FCSTD DOCUMENT  (FreeCAD 0.17R13541 (Git))
Label: PCSchrank2
License: All rights reserved
LicenseURL: http://en.wikipedia.org/wiki/All_rights_reserved
objects: Drawing::FeatureViewPython×69, Drawing::FeatureViewPart×29, Part::Box×21, Drawing::FeaturePage×5, Part::Cylinder×4, App::Part×2, Part::FeaturePython×1
note: 26 computed .brp shape members not serialized (recipe doc carries the construction recipe); baked Part::Feature solids carry a one-line shape summary decoded from their .brp

FEATURE [Part::Box] Box  label="Boden"
  AttacherType = Attacher::AttachEngine3D
  Height = 19
  Length = 750
  Width = 300
FEATURE [Part::Box] Box001  label="Mittelebene"
  AttacherType = Attacher::AttachEngine3D
  Height = 19
  Length = 731
  Placement = pos=(0,0,700) rot=(0,0,1;0rad)
  Width = 300
FEATURE [Part::Box] Box002  label="Deckel"
  AttacherType = Attacher::AttachEngine3D
  Height = 19
  Length = 731
  Placement = pos=(0,0,1281) rot=(0,0,1;0rad)
  Width = 300
FEATURE [Part::Box] Box003  label="SeiteLi"
  AttacherType = Attacher::AttachEngine3D
  Height = 1300
  Length = 19
  Placement = pos=(-19,0,0) rot=(0,0,1;0rad)
  Width = 300
FEATURE [Part::Box] Box004  label="SeiteRe"
  AttacherType = Attacher::AttachEngine3D
  Height = 600
  Length = 19
  Placement = pos=(731,0,700) rot=(0,0,1;0rad)
  Width = 300
FEATURE [Part::Box] Box005  label="AbdeckungVo"
  AttacherType = Attacher::AttachEngine3D
  Height = 705
  Length = 550
  Placement = pos=(200,-19,0) rot=(0,0,1;0rad)
  Width = 19
FEATURE [Part::Box] Box006  label="Tuere"
  AttacherType = Attacher::AttachEngine3D
  Height = 705
  Length = 219
  Placement = pos=(-19,-19,0) rot=(0,0,1;0rad)
  Width = 19
FEATURE [Part::Box] Box007  label="StuetzeMi"
  AttacherType = Attacher::AttachEngine3D
  Height = 681
  Length = 19
  Placement = pos=(190,0,19) rot=(0,0,1;0rad)
  Width = 300
FEATURE [Part::Box] Box008  label="Klappe"
  AttacherType = Attacher::AttachEngine3D
  Height = 595
  Length = 769
  Placement = pos=(-19,-19,705) rot=(0,0,1;0rad)
  Width = 19
FEATURE [Part::Box] Box009  label="StuetzeHi"
  AttacherType = Attacher::AttachEngine3D
  Height = 681
  Length = 100
  Placement = pos=(650,281,19) rot=(0,0,1;0rad)
  Width = 19
FEATURE [Part::Cylinder] Cylinder  label="GriffTuere"
  Angle = 360
  AttacherType = Attacher::AttachEngine3D
  Height = 20
  Placement = pos=(160,-19,600) rot=(1,0,0;1.5708rad)
  Radius = 10
FEATURE [Part::Cylinder] Cylinder001  label="GriffKlappe"
  Angle = 360
  AttacherType = Attacher::AttachEngine3D
  Height = 20
  Placement = pos=(380,-19,1200) rot=(1,0,0;1.5708rad)
  Radius = 10
FEATURE [App::Part] Part
  Group = -> [Box,Box001,Box002,Box003,Box004,Box005,Box006,Box007,Box008,Box009,Cylinder,Cylinder001]
  License = CC BY 3.0
  LicenseURL = http://creativecommons.org/licenses/by/3.0/
  Origin = -> Origin
FEATURE [Part::Box] Box010  label="Boden001"
  AttacherType = Attacher::AttachEngine3D
  Height = 19
  Length = 750
  Width = 300
FEATURE [Part::Box] Box011  label="Mittelebene001"
  AttacherType = Attacher::AttachEngine3D
  Height = 19
  Length = 731
  Placement = pos=(0,0,700) rot=(0,0,1;0rad)
  Width = 300
FEATURE [Part::Box] Box012  label="Deckel001"
  AttacherType = Attacher::AttachEngine3D
  Height = 19
  Length = 731
  Placement = pos=(0,0,1281) rot=(0,0,1;0rad)
  Width = 300
FEATURE [Part::Box] Box013  label="SeiteLi001"
  AttacherType = Attacher::AttachEngine3D
  Height = 1300
  Length = 19
  Placement = pos=(-19,0,0) rot=(0,0,1;0rad)
  Width = 300
FEATURE [Part::Box] Box014  label="SeiteRe001"
  AttacherType = Attacher::AttachEngine3D
  Height = 600
  Length = 19
  Placement = pos=(731,0,700) rot=(0,0,1;0rad)
  Width = 300
FEATURE [Part::Box] Box015  label="AbdeckungVo001"
  AttacherType = Attacher::AttachEngine3D
  Height = 705
  Length = 550
  Placement = pos=(200,-19,0) rot=(0,0,1;0rad)
  Width = 19
FEATURE [Part::Box] Box016  label="Tuere001"
  AttacherType = Attacher::AttachEngine3D
  Height = 705
  Length = 219
  Placement = pos=(-19,-19,0) rot=(0,0,1;0rad)
  Width = 19
FEATURE [Part::Box] Box017  label="StuetzeMi001"
  AttacherType = Attacher::AttachEngine3D
  Height = 681
  Length = 19
  Placement = pos=(190,0,19) rot=(0,0,1;0rad)
  Width = 300
FEATURE [Part::Box] Box018  label="Klappe001"
  AttacherType = Attacher::AttachEngine3D
  Height = 595
  Length = 769
  Placement = pos=(-19,-19,705) rot=(0,0,1;0rad)
  Width = 19
FEATURE [Part::Box] Box019  label="StuetzeHi001"
  AttacherType = Attacher::AttachEngine3D
  Height = 681
  Length = 100
  Placement = pos=(650,281,19) rot=(0,0,1;0rad)
  Width = 19
FEATURE [Part::Cylinder] Cylinder002  label="GriffTuere001"
  Angle = 360
  AttacherType = Attacher::AttachEngine3D
  Height = 20
  Placement = pos=(160,-19,600) rot=(1,0,0;1.5708rad)
  Radius = 10
FEATURE [Part::Cylinder] Cylinder003  label="GriffKlappe001"
  Angle = 360
  AttacherType = Attacher::AttachEngine3D
  Height = 20
  Placement = pos=(380,-19,1200) rot=(1,0,0;1.5708rad)
  Radius = 10
FEATURE [App::Part] Part001
  Group = -> [Box010,Box011,Box012,Box013,Box014,Box015,Box016,Box017,Box018,Box019,Cylinder002,Cylinder003]
  License = CC BY 3.0
  LicenseURL = http://creativecommons.org/licenses/by/3.0/
  Origin = -> Origin001
FEATURE [Drawing::FeatureViewPart] Ortho  label="Ortho_0_0"
  Direction = (0,0,1)
  HiddenWidth = 0.15
  LineWidth = 0.35
  Rotation = 0
  Scale = 0.1
  ShowHiddenLines = false
  ShowSmoothLines = false
  Source = -> Box
  Tolerance = 0.05
  ViewResult = <g id="Ortho_0_0"\n   transform="rotate(0,32.5,55) translate(32.5,55) scale(0.1,0.1)"\n  >\n<g   fill="none"\n   stroke="rgb(0, 0, 0)"\n   stroke-linecap="butt"\n   stroke-linejoin="miter"\n   stroke-width="3.500000"\n   transform="scale(1,-1)"\n  >\n<path id= "1" d=" M 0 0 L 0 300 " />\n<path id= "2" d=" M 750 0 L 750 300 " />\n<path id= "3" d=" M 0 0 L 750 0 " />\n<path id= "4" d=" M 0 300 L 750 300 " />\n</g>\n</g>
  Visible = true
  X = 32.5
  Y = 55
FEATURE [Drawing::FeatureViewPython] dim001  # drawing view (typed FeaturePython)
  Rotation = 0
  ViewResult = <g> \n  <line x1="32.500000" y1="57.000000" x2="32.500000" y2="64.603174" style="stroke:rgb(0,0,255);stroke-width:0.50" />\n<line x1="107.500000" y1="57.000000" x2="107.500000" y2="64.603174" style="stroke:rgb(0,0,255);stroke-width:0.50" />\n<line x1="32.500000" y1="63.603174" x2="107.500000" y2="63.603174" style="stroke:rgb(0,0,255);stroke-width:0.50" /> \n  <polygon points="107.500000,63.603174 104.500000,62.603174 103.500000,63.603174 104.500000,64.603174" style="fill:rgb(0,0,255);stroke:rgb(0,0,255);stroke-width:0" /><polygon points="32.500000,63.603174 35.500000,64.603174 36.500000,63.603174 35.500000,62.603174" style="fill:rgb(0,0,255);stroke:rgb(0,0,255);stroke-width:0" /> \n  <text x="70.000000" y="61.603174" font-family="inherit" font-size="3.6" fill="rgb(0,0,255)" text-anchor="middle" transform="rotate(0.000000 70.000000,61.603174)" >750</text> </g>
  Visible = true
  X = 0
  Y = 0
  arrowL1 = 3
  arrowL2 = 1
  arrowW = 2
  arrow_scheme = 0
  autoPlaceOffset = 2
  autoPlaceText = true
  click1_x = 54.517
  click1_y = 63.6032
  click2_x = 54.517
  click2_y = 63.6032
  comma_decimal_place = false
  dimension_line_overshoot = 1
  gap_datum_points = 2
  halfDimension_linear = false
  lineColor = rgb(0,0,255)
  strokeWidth = 0.5
  textFormat_linear = %(value)3.3f
  textRenderer_color = rgb(0,0,255)
  textRenderer_family = inherit
  textRenderer_size = 3.6
  unit_custom_scale = 1
  unit_scheme = 0
FEATURE [Drawing::FeatureViewPython] dim002  # drawing view (typed FeaturePython)
  Rotation = 0
  ViewResult = <g> \n  <line x1="109.500000" y1="55.000000" x2="116.280753" y2="55.000000" style="stroke:rgb(0,0,255);stroke-width:0.50" />\n<line x1="109.500000" y1="25.000000" x2="116.280753" y2="25.000000" style="stroke:rgb(0,0,255);stroke-width:0.50" />\n<line x1="115.280753" y1="55.000000" x2="115.280753" y2="25.000000" style="stroke:rgb(0,0,255);stroke-width:0.50" /> \n  <polygon points="115.280753,25.000000 114.280753,28.000000 115.280753,29.000000 116.280753,28.000000" style="fill:rgb(0,0,255);stroke:rgb(0,0,255);stroke-width:0" /><polygon points="115.280753,55.000000 116.280753,52.000000 115.280753,51.000000 114.280753,52.000000" style="fill:rgb(0,0,255);stroke:rgb(0,0,255);stroke-width:0" /> \n  <text x="113.280753" y="40.000000" font-family="inherit" font-size="3.6" fill="rgb(0,0,255)" text-anchor="middle" transform="rotate(-90.000000 113.280753,40.000000)" >300</text> </g>
  Visible = true
  X = 0
  Y = 0
  arrowL1 = 3
  arrowL2 = 1
  arrowW = 2
  arrow_scheme = 0
  autoPlaceOffset = 2
  autoPlaceText = true
  click1_x = 115.281
  click1_y = 42.0235
  click2_x = 115.281
  click2_y = 42.0235
  comma_decimal_place = false
  dimension_line_overshoot = 1
  gap_datum_points = 2
  halfDimension_linear = false
  lineColor = rgb(0,0,255)
  strokeWidth = 0.5
  textFormat_linear = %(value)3.3f
  textRenderer_color = rgb(0,0,255)
  textRenderer_family = inherit
  textRenderer_size = 3.6
  unit_custom_scale = 1
  unit_scheme = 0
FEATURE [Drawing::FeatureViewPart] Ortho001  label="Ortho_0_001"
  Direction = (0,0,1)
  HiddenWidth = 0.15
  LineWidth = 0.35
  Rotation = 0
  Scale = 0.1
  ShowHiddenLines = false
  ShowSmoothLines = false
  Source = -> Box001
  Tolerance = 0.05
  ViewResult = <g id="Ortho_0_001"\n   transform="rotate(0,33.45,105) translate(33.45,105) scale(0.1,0.1)"\n  >\n<g   fill="none"\n   stroke="rgb(0, 0, 0)"\n   stroke-linecap="butt"\n   stroke-linejoin="miter"\n   stroke-width="3.500000"\n   transform="scale(1,-1)"\n  >\n<path id= "1" d=" M 0 0 L 0 300 " />\n<path id= "2" d=" M 731 0 L 731 300 " />\n<path id= "3" d=" M 0 0 L 731 0 " />\n<path id= "4" d=" M 0 300 L 731 300 " />\n</g>\n</g>
  Visible = true
  X = 33.45
  Y = 105
FEATURE [Drawing::FeatureViewPython] dim003  # drawing view (typed FeaturePython)
  Rotation = 0
  ViewResult = <g> \n  <line x1="33.450000" y1="107.000000" x2="33.450000" y2="114.577097" style="stroke:rgb(0,0,255);stroke-width:0.50" />\n<line x1="106.550000" y1="107.000000" x2="106.550000" y2="114.577097" style="stroke:rgb(0,0,255);stroke-width:0.50" />\n<line x1="33.450000" y1="113.577097" x2="106.550000" y2="113.577097" style="stroke:rgb(0,0,255);stroke-width:0.50" /> \n  <polygon points="106.550000,113.577097 103.550000,112.577097 102.550000,113.577097 103.550000,114.577097" style="fill:rgb(0,0,255);stroke:rgb(0,0,255);stroke-width:0" /><polygon points="33.450000,113.577097 36.450000,114.577097 37.450000,113.577097 36.450000,112.577097" style="fill:rgb(0,0,255);stroke:rgb(0,0,255);stroke-width:0" /> \n  <text x="70.000000" y="111.577097" font-family="inherit" font-size="3.6" fill="rgb(0,0,255)" text-anchor="middle" transform="rotate(0.000000 70.000000,111.577097)" >731</text> </g>
  Visible = true
  X = 0
  Y = 0
  arrowL1 = 3
  arrowL2 = 1
  arrowW = 2
  arrow_scheme = 0
  autoPlaceOffset = 2
  autoPlaceText = true
  click1_x = 56.2207
  click1_y = 113.577
  click2_x = 56.2207
  click2_y = 113.577
  comma_decimal_place = false
  dimension_line_overshoot = 1
  gap_datum_points = 2
  halfDimension_linear = false
  lineColor = rgb(0,0,255)
  strokeWidth = 0.5
  textFormat_linear = %(value)3.3f
  textRenderer_color = rgb(0,0,255)
  textRenderer_family = inherit
  textRenderer_size = 3.6
  unit_custom_scale = 1
  unit_scheme = 0
FEATURE [Drawing::FeatureViewPython] dim004  # drawing view (typed FeaturePython)
  Rotation = 0
  ViewResult = <g> \n  <line x1="108.550000" y1="105.000000" x2="116.848639" y2="105.000000" style="stroke:rgb(0,0,255);stroke-width:0.50" />\n<line x1="108.550000" y1="75.000000" x2="116.848639" y2="75.000000" style="stroke:rgb(0,0,255);stroke-width:0.50" />\n<line x1="115.848639" y1="105.000000" x2="115.848639" y2="75.000000" style="stroke:rgb(0,0,255);stroke-width:0.50" /> \n  <polygon points="115.848639,75.000000 114.848639,78.000000 115.848639,79.000000 116.848639,78.000000" style="fill:rgb(0,0,255);stroke:rgb(0,0,255);stroke-width:0" /><polygon points="115.848639,105.000000 116.848639,102.000000 115.848639,101.000000 114.848639,102.000000" style="fill:rgb(0,0,255);stroke:rgb(0,0,255);stroke-width:0" /> \n  <text x="113.848639" y="90.000000" font-family="inherit" font-size="3.6" fill="rgb(0,0,255)" text-anchor="middle" transform="rotate(-90.000000 113.848639,90.000000)" >300</text> </g>
  Visible = true
  X = 0
  Y = 0
  arrowL1 = 3
  arrowL2 = 1
  arrowW = 2
  arrow_scheme = 0
  autoPlaceOffset = 2
  autoPlaceText = true
  click1_x = 115.849
  click1_y = 87.4544
  click2_x = 115.849
  click2_y = 87.4544
  comma_decimal_place = false
  dimension_line_overshoot = 1
  gap_datum_points = 2
  halfDimension_linear = false
  lineColor = rgb(0,0,255)
  strokeWidth = 0.5
  textFormat_linear = %(value)3.3f
  textRenderer_color = rgb(0,0,255)
  textRenderer_family = inherit
  textRenderer_size = 3.6
  unit_custom_scale = 1
  unit_scheme = 0
FEATURE [Drawing::FeatureViewPart] Ortho002  label="Ortho_0_002"
  Direction = (0,0,1)
  HiddenWidth = 0.15
  LineWidth = 0.35
  Rotation = 0
  Scale = 0.1
  ShowHiddenLines = false
  ShowSmoothLines = false
  Source = -> Box002
  Tolerance = 0.05
  ViewResult = <g id="Ortho_0_002"\n   transform="rotate(0,33.45,155) translate(33.45,155) scale(0.1,0.1)"\n  >\n<g   fill="none"\n   stroke="rgb(0, 0, 0)"\n   stroke-linecap="butt"\n   stroke-linejoin="miter"\n   stroke-width="3.500000"\n   transform="scale(1,-1)"\n  >\n<path id= "1" d=" M 0 0 L 0 300 " />\n<path id= "2" d=" M 731 0 L 731 300 " />\n<path id= "3" d=" M 0 0 L 731 0 " />\n<path id= "4" d=" M 0 300 L 731 300 " />\n</g>\n</g>
  Visible = true
  X = 33.45
  Y = 155
FEATURE [Drawing::FeatureViewPython] dim005  # drawing view (typed FeaturePython)
  Rotation = 0
  ViewResult = <g> \n  <line x1="33.450000" y1="157.000000" x2="33.450000" y2="165.686790" style="stroke:rgb(0,0,255);stroke-width:0.50" />\n<line x1="106.550000" y1="157.000000" x2="106.550000" y2="165.686790" style="stroke:rgb(0,0,255);stroke-width:0.50" />\n<line x1="33.450000" y1="164.686790" x2="106.550000" y2="164.686790" style="stroke:rgb(0,0,255);stroke-width:0.50" /> \n  <polygon points="106.550000,164.686790 103.550000,163.686790 102.550000,164.686790 103.550000,165.686790" style="fill:rgb(0,0,255);stroke:rgb(0,0,255);stroke-width:0" /><polygon points="33.450000,164.686790 36.450000,165.686790 37.450000,164.686790 36.450000,163.686790" style="fill:rgb(0,0,255);stroke:rgb(0,0,255);stroke-width:0" /> \n  <text x="70.000000" y="162.686790" font-family="inherit" font-size="3.6" fill="rgb(0,0,255)" text-anchor="middle" transform="rotate(0.000000 70.000000,162.686790)" >731</text> </g>
  Visible = true
  X = 0
  Y = 0
  arrowL1 = 3
  arrowL2 = 1
  arrowW = 2
  arrow_scheme = 0
  autoPlaceOffset = 2
  autoPlaceText = true
  click1_x = 62.4674
  click1_y = 164.687
  click2_x = 62.4674
  click2_y = 164.687
  comma_decimal_place = false
  dimension_line_overshoot = 1
  gap_datum_points = 2
  halfDimension_linear = false
  lineColor = rgb(0,0,255)
  strokeWidth = 0.5
  textFormat_linear = %(value)3.3f
  textRenderer_color = rgb(0,0,255)
  textRenderer_family = inherit
  textRenderer_size = 3.6
  unit_custom_scale = 1
  unit_scheme = 0
FEATURE [Drawing::FeatureViewPython] dim006  # drawing view (typed FeaturePython)
  Rotation = 0
  ViewResult = <g> \n  <line x1="108.550000" y1="155.000000" x2="116.848639" y2="155.000000" style="stroke:rgb(0,0,255);stroke-width:0.50" />\n<line x1="108.550000" y1="125.000000" x2="116.848639" y2="125.000000" style="stroke:rgb(0,0,255);stroke-width:0.50" />\n<line x1="115.848639" y1="155.000000" x2="115.848639" y2="125.000000" style="stroke:rgb(0,0,255);stroke-width:0.50" /> \n  <polygon points="115.848639,125.000000 114.848639,128.000000 115.848639,129.000000 116.848639,128.000000" style="fill:rgb(0,0,255);stroke:rgb(0,0,255);stroke-width:0" /><polygon points="115.848639,155.000000 116.848639,152.000000 115.848639,151.000000 114.848639,152.000000" style="fill:rgb(0,0,255);stroke:rgb(0,0,255);stroke-width:0" /> \n  <text x="113.848639" y="140.000000" font-family="inherit" font-size="3.6" fill="rgb(0,0,255)" text-anchor="middle" transform="rotate(-90.000000 113.848639,140.000000)" >300</text> </g>
  Visible = true
  X = 0
  Y = 0
  arrowL1 = 3
  arrowL2 = 1
  arrowW = 2
  arrow_scheme = 0
  autoPlaceOffset = 2
  autoPlaceText = true
  click1_x = 115.849
  click1_y = 140.836
  click2_x = 115.849
  click2_y = 140.836
  comma_decimal_place = false
  dimension_line_overshoot = 1
  gap_datum_points = 2
  halfDimension_linear = false
  lineColor = rgb(0,0,255)
  strokeWidth = 0.5
  textFormat_linear = %(value)3.3f
  textRenderer_color = rgb(0,0,255)
  textRenderer_family = inherit
  textRenderer_size = 3.6
  unit_custom_scale = 1
  unit_scheme = 0
FEATURE [Drawing::FeatureViewPart] Ortho003  label="Ortho_0_003"
  Direction = (1,0,0)
  HiddenWidth = 0.15
  LineWidth = 0.35
  Rotation = -90
  Scale = 0.1
  ShowHiddenLines = false
  ShowSmoothLines = false
  Source = -> Box003
  Tolerance = 0.05
  ViewResult = <g id="Ortho_0_003"\n   transform="rotate(-90,145,155) translate(145,155) scale(0.1,0.1)"\n  >\n<g   fill="none"\n   stroke="rgb(0, 0, 0)"\n   stroke-linecap="butt"\n   stroke-linejoin="miter"\n   stroke-width="3.500000"\n   transform="scale(1,-1)"\n  >\n<path id= "1" d=" M 0 0 L 1300 0 " />\n<path id= "2" d=" M 1300 0 L 1300 -300 " />\n<path id= "3" d=" M 0 -300 L 1300 -300 " />\n<path id= "4" d=" M 0 0 L 0 -300 " />\n</g>\n</g>
  Visible = true
  X = 145
  Y = 155
FEATURE [Drawing::FeatureViewPython] dim007  # drawing view (typed FeaturePython)
  Rotation = 0
  ViewResult = <g> \n  <line x1="145.000000" y1="157.000000" x2="145.000000" y2="166.254676" style="stroke:rgb(0,0,255);stroke-width:0.50" />\n<line x1="175.000000" y1="157.000000" x2="175.000000" y2="166.254676" style="stroke:rgb(0,0,255);stroke-width:0.50" />\n<line x1="145.000000" y1="165.254676" x2="175.000000" y2="165.254676" style="stroke:rgb(0,0,255);stroke-width:0.50" /> \n  <polygon points="175.000000,165.254676 172.000000,164.254676 171.000000,165.254676 172.000000,166.254676" style="fill:rgb(0,0,255);stroke:rgb(0,0,255);stroke-width:0" /><polygon points="145.000000,165.254676 148.000000,166.254676 149.000000,165.254676 148.000000,164.254676" style="fill:rgb(0,0,255);stroke:rgb(0,0,255);stroke-width:0" /> \n  <text x="160.000000" y="163.254676" font-family="inherit" font-size="3.6" fill="rgb(0,0,255)" text-anchor="middle" transform="rotate(0.000000 160.000000,163.254676)" >300</text> </g>
  Visible = true
  X = 0
  Y = 0
  arrowL1 = 3
  arrowL2 = 1
  arrowW = 2
  arrow_scheme = 0
  autoPlaceOffset = 2
  autoPlaceText = true
  click1_x = 159.008
  click1_y = 165.255
  click2_x = 159.008
  click2_y = 165.255
  comma_decimal_place = false
  dimension_line_overshoot = 1
  gap_datum_points = 2
  halfDimension_linear = false
  lineColor = rgb(0,0,255)
  strokeWidth = 0.5
  textFormat_linear = %(value)3.3f
  textRenderer_color = rgb(0,0,255)
  textRenderer_family = inherit
  textRenderer_size = 3.6
  unit_custom_scale = 1
  unit_scheme = 0
FEATURE [Drawing::FeatureViewPython] dim008  # drawing view (typed FeaturePython)
  Rotation = 0
  ViewResult = <g> \n  <line x1="177.000000" y1="155.000000" x2="186.698553" y2="155.000000" style="stroke:rgb(0,0,255);stroke-width:0.50" />\n<line x1="177.000000" y1="25.000000" x2="186.698553" y2="25.000000" style="stroke:rgb(0,0,255);stroke-width:0.50" />\n<line x1="185.698553" y1="155.000000" x2="185.698553" y2="25.000000" style="stroke:rgb(0,0,255);stroke-width:0.50" /> \n  <polygon points="185.698553,25.000000 184.698553,28.000000 185.698553,29.000000 186.698553,28.000000" style="fill:rgb(0,0,255);stroke:rgb(0,0,255);stroke-width:0" /><polygon points="185.698553,155.000000 186.698553,152.000000 185.698553,151.000000 184.698553,152.000000" style="fill:rgb(0,0,255);stroke:rgb(0,0,255);stroke-width:0" /> \n  <text x="183.698553" y="90.000000" font-family="inherit" font-size="3.6" fill="rgb(0,0,255)" text-anchor="middle" transform="rotate(-90.000000 183.698553,90.000000)" >1300</text> </g>
  Visible = true
  X = 0
  Y = 0
  arrowL1 = 3
  arrowL2 = 1
  arrowW = 2
  arrow_scheme = 0
  autoPlaceOffset = 2
  autoPlaceText = true
  click1_x = 185.699
  click1_y = 129.478
  click2_x = 185.699
  click2_y = 129.478
  comma_decimal_place = false
  dimension_line_overshoot = 1
  gap_datum_points = 2
  halfDimension_linear = false
  lineColor = rgb(0,0,255)
  strokeWidth = 0.5
  textFormat_linear = %(value)3.3f
  textRenderer_color = rgb(0,0,255)
  textRenderer_family = inherit
  textRenderer_size = 3.6
  unit_custom_scale = 1
  unit_scheme = 0
FEATURE [Drawing::FeatureViewPart] Ortho004  label="Ortho_0_004"
  Direction = (1,0,0)
  HiddenWidth = 0.15
  LineWidth = 0.35
  Rotation = 0
  Scale = 0.1
  ShowHiddenLines = false
  ShowSmoothLines = false
  Source = -> Box004
  Tolerance = 0.05
  ViewResult = <g id="Ortho_0_004"\n   transform="rotate(0,50,175) translate(50,175) scale(0.1,0.1)"\n  >\n<g   fill="none"\n   stroke="rgb(0, 0, 0)"\n   stroke-linecap="butt"\n   stroke-linejoin="miter"\n   stroke-width="3.500000"\n   transform="scale(1,-1)"\n  >\n<path id= "1" d=" M 700 0 L 1300 0 " />\n<path id= "2" d=" M 1300 0 L 1300 -300 " />\n<path id= "3" d=" M 700 -300 L 1300 -300 " />\n<path id= "4" d=" M 700 0 L 700 -300 " />\n</g>\n</g>
  Visible = true
  X = 50
  Y = 175
FEATURE [Drawing::FeatureViewPython] dim009  # drawing view (typed FeaturePython)
  Rotation = 0
  ViewResult = <g> \n  <line x1="120.000000" y1="207.000000" x2="120.000000" y2="213.389171" style="stroke:rgb(0,0,255);stroke-width:0.50" />\n<line x1="180.000000" y1="207.000000" x2="180.000000" y2="213.389171" style="stroke:rgb(0,0,255);stroke-width:0.50" />\n<line x1="120.000000" y1="212.389171" x2="180.000000" y2="212.389171" style="stroke:rgb(0,0,255);stroke-width:0.50" /> \n  <polygon points="180.000000,212.389171 177.000000,211.389171 176.000000,212.389171 177.000000,213.389171" style="fill:rgb(0,0,255);stroke:rgb(0,0,255);stroke-width:0" /><polygon points="120.000000,212.389171 123.000000,213.389171 124.000000,212.389171 123.000000,211.389171" style="fill:rgb(0,0,255);stroke:rgb(0,0,255);stroke-width:0" /> \n  <text x="150.000000" y="210.389171" font-family="inherit" font-size="3.6" fill="rgb(0,0,255)" text-anchor="middle" transform="rotate(0.000000 150.000000,210.389171)" >600</text> </g>
  Visible = true
  X = 0
  Y = 0
  arrowL1 = 3
  arrowL2 = 1
  arrowW = 2
  arrow_scheme = 0
  autoPlaceOffset = 2
  autoPlaceText = true
  click1_x = 140.836
  click1_y = 212.389
  click2_x = 140.836
  click2_y = 212.389
  comma_decimal_place = false
  dimension_line_overshoot = 1
  gap_datum_points = 2
  halfDimension_linear = false
  lineColor = rgb(0,0,255)
  strokeWidth = 0.5
  textFormat_linear = %(value)3.3f
  textRenderer_color = rgb(0,0,255)
  textRenderer_family = inherit
  textRenderer_size = 3.6
  unit_custom_scale = 1
  unit_scheme = 0
FEATURE [Drawing::FeatureViewPython] dim010  # drawing view (typed FeaturePython)
  Rotation = 0
  ViewResult = <g> \n  <line x1="182.000000" y1="175.000000" x2="190.673751" y2="175.000000" style="stroke:rgb(0,0,255);stroke-width:0.50" />\n<line x1="182.000000" y1="205.000000" x2="190.673751" y2="205.000000" style="stroke:rgb(0,0,255);stroke-width:0.50" />\n<line x1="189.673751" y1="175.000000" x2="189.673751" y2="205.000000" style="stroke:rgb(0,0,255);stroke-width:0.50" /> \n  <polygon points="189.673751,205.000000 190.673751,202.000000 189.673751,201.000000 188.673751,202.000000" style="fill:rgb(0,0,255);stroke:rgb(0,0,255);stroke-width:0" /><polygon points="189.673751,175.000000 188.673751,178.000000 189.673751,179.000000 190.673751,178.000000" style="fill:rgb(0,0,255);stroke:rgb(0,0,255);stroke-width:0" /> \n  <text x="187.673751" y="190.000000" font-family="inherit" font-size="3.6" fill="rgb(0,0,255)" text-anchor="middle" transform="rotate(-90.000000 187.673751,190.000000)" >300</text> </g>
  Visible = true
  X = 0
  Y = 0
  arrowL1 = 3
  arrowL2 = 1
  arrowW = 2
  arrow_scheme = 0
  autoPlaceOffset = 2
  autoPlaceText = true
  click1_x = 189.674
  click1_y = 191.377
  click2_x = 189.674
  click2_y = 191.377
  comma_decimal_place = false
  dimension_line_overshoot = 1
  gap_datum_points = 2
  halfDimension_linear = false
  lineColor = rgb(0,0,255)
  strokeWidth = 0.5
  textFormat_linear = %(value)3.3f
  textRenderer_color = rgb(0,0,255)
  textRenderer_family = inherit
  textRenderer_size = 3.6
  unit_custom_scale = 1
  unit_scheme = 0
FEATURE [Drawing::FeatureViewPython] text001  # drawing view (typed FeaturePython)
  Rotation = 0
  ViewResult = <g> <text x="52.245464" y="41.455640" font-family="inherit" font-size="5" fill="rgb(0,0,0)" text-anchor="inherit" transform="rotate(0.000000 52.245464,41.455640)" >Boden</text> </g>
  Visible = true
  X = 0
  Y = 0
  click1_x = 52.2455
  click1_y = 41.4556
  rotation = 0
  text = Boden
  textRenderer_addText_color = rgb(0,0,0)
  textRenderer_addText_family = inherit
  textRenderer_addText_size = 5
FEATURE [Drawing::FeatureViewPython] text002  # drawing view (typed FeaturePython)
  Rotation = 0
  ViewResult = <g> <text x="53.949121" y="90.293792" font-family="inherit" font-size="5" fill="rgb(0,0,0)" text-anchor="inherit" transform="rotate(0.000000 53.949121,90.293792)" >Mittelboden</text> </g>
  Visible = true
  X = 0
  Y = 0
  click1_x = 53.9491
  click1_y = 90.2938
  rotation = 0
  text = Mittelboden
  textRenderer_addText_color = rgb(0,0,0)
  textRenderer_addText_family = inherit
  textRenderer_addText_size = 5
FEATURE [Drawing::FeatureViewPython] text003  # drawing view (typed FeaturePython)
  Rotation = 0
  ViewResult = <g> <text x="56.220663" y="140.267714" font-family="inherit" font-size="5" fill="rgb(0,0,0)" text-anchor="inherit" transform="rotate(0.000000 56.220663,140.267714)" >Deckel</text> </g>
  Visible = true
  X = 0
  Y = 0
  click1_x = 56.2207
  click1_y = 140.268
  rotation = 0
  text = Deckel
  textRenderer_addText_color = rgb(0,0,0)
  textRenderer_addText_family = inherit
  textRenderer_addText_size = 5
FEATURE [Drawing::FeatureViewPython] text004  # drawing view (typed FeaturePython)
  Rotation = 0
  ViewResult = <g> <text x="160.000000" y="110.000000" font-family="inherit" font-size="5" fill="rgb(0,0,0)" text-anchor="inherit" transform="rotate(270.000000 160.000000,110.000000)" >Seitenwand links</text> </g>
  Visible = true
  X = 0
  Y = 0
  click1_x = 160
  click1_y = 110
  rotation = 270
  text = Seitenwand links
  textRenderer_addText_color = rgb(0,0,0)
  textRenderer_addText_family = inherit
  textRenderer_addText_size = 5
FEATURE [Drawing::FeatureViewPython] text005  # drawing view (typed FeaturePython)
  Rotation = 0
  ViewResult = <g> <text x="130.000000" y="190.000000" font-family="inherit" font-size="5" fill="rgb(0,0,0)" text-anchor="inherit" transform="rotate(0.000000 130.000000,190.000000)" >Seitenwand rechts</text> </g>
  Visible = true
  X = 0
  Y = 0
  click1_x = 130
  click1_y = 190
  rotation = 0
  text = Seitenwand rechts
  textRenderer_addText_color = rgb(0,0,0)
  textRenderer_addText_family = inherit
  textRenderer_addText_size = 5
FEATURE [Drawing::FeaturePage] Page  label="Seite"
  EditableTexts = Manuel Dillmann	 | PC-Schrank | Böden  | Seitenwände | A4 | 1 / X | 0.1 | ... | ... | 17/04/2019 | REV A
  Group = -> [Ortho,dim001,dim002,Ortho001,dim003,dim004,Ortho002,dim005,dim006,Ortho003,dim007,dim008,Ortho004,dim009,dim010,text001,text002,text003,text004,text005]
  Template = C:/Program Files/FreeCAD 0.17/data/Mod/Drawing/Templates/A4_Portrait_ISO7200.svg
FEATURE [Drawing::FeatureViewPart] Ortho005  label="Ortho_0_005"
  Direction = (0,1,0)
  HiddenWidth = 0.15
  LineWidth = 0.35
  Rotation = 90
  Scale = 0.1
  ShowHiddenLines = false
  ShowSmoothLines = false
  Source = -> Box005
  Tolerance = 0.05
  ViewResult = <g id="Ortho_0_005"\n   transform="rotate(90,12.5,24.75) translate(12.5,24.75) scale(0.1,0.1)"\n  >\n<g   fill="none"\n   stroke="rgb(0, 0, 0)"\n   stroke-linecap="butt"\n   stroke-linejoin="miter"\n   stroke-width="3.500000"\n   transform="scale(1,-1)"\n  >\n<path id= "1" d=" M 0 200 L 705 200 " />\n<path id= "2" d=" M 0 750 L 705 750 " />\n<path id= "3" d=" M 0 200 L 0 750 " />\n<path id= "4" d=" M 705 200 L 705 750 " />\n</g>\n</g>
  Visible = true
  X = 12.5
  Y = 24.75
FEATURE [Drawing::FeatureViewPython] dim011  # drawing view (typed FeaturePython)
  Rotation = 0
  ViewResult = <g> \n  <line x1="32.500000" y1="97.250000" x2="32.500000" y2="106.626700" style="stroke:rgb(0,0,255);stroke-width:0.50" />\n<line x1="87.500000" y1="97.250000" x2="87.500000" y2="106.626700" style="stroke:rgb(0,0,255);stroke-width:0.50" />\n<line x1="32.500000" y1="105.626700" x2="87.500000" y2="105.626700" style="stroke:rgb(0,0,255);stroke-width:0.50" /> \n  <polygon points="87.500000,105.626700 84.500000,104.626700 83.500000,105.626700 84.500000,106.626700" style="fill:rgb(0,0,255);stroke:rgb(0,0,255);stroke-width:0" /><polygon points="32.500000,105.626700 35.500000,106.626700 36.500000,105.626700 35.500000,104.626700" style="fill:rgb(0,0,255);stroke:rgb(0,0,255);stroke-width:0" /> \n  <text x="60.000000" y="103.626700" font-family="inherit" font-size="3.6" fill="rgb(0,0,255)" text-anchor="middle" transform="rotate(0.000000 60.000000,103.626700)" >550</text> </g>
  Visible = true
  X = 0
  Y = 0
  arrowL1 = 3
  arrowL2 = 1
  arrowW = 2
  arrow_scheme = 0
  autoPlaceOffset = 2
  autoPlaceText = true
  click1_x = 52.2455
  click1_y = 105.627
  click2_x = 52.2455
  click2_y = 105.627
  comma_decimal_place = false
  dimension_line_overshoot = 1
  gap_datum_points = 2
  halfDimension_linear = false
  lineColor = rgb(0,0,255)
  strokeWidth = 0.5
  textFormat_linear = %(value)3.3f
  textRenderer_color = rgb(0,0,255)
  textRenderer_family = inherit
  textRenderer_size = 3.6
  unit_custom_scale = 1
  unit_scheme = 0
FEATURE [Drawing::FeatureViewPython] dim012  # drawing view (typed FeaturePython)
  Rotation = 0
  ViewResult = <g> \n  <line x1="89.500000" y1="24.750000" x2="99.244189" y2="24.750000" style="stroke:rgb(0,0,255);stroke-width:0.50" />\n<line x1="89.500000" y1="95.250000" x2="99.244189" y2="95.250000" style="stroke:rgb(0,0,255);stroke-width:0.50" />\n<line x1="98.244189" y1="24.750000" x2="98.244189" y2="95.250000" style="stroke:rgb(0,0,255);stroke-width:0.50" /> \n  <polygon points="98.244189,95.250000 99.244189,92.250000 98.244189,91.250000 97.244189,92.250000" style="fill:rgb(0,0,255);stroke:rgb(0,0,255);stroke-width:0" /><polygon points="98.244189,24.750000 97.244189,27.750000 98.244189,28.750000 99.244189,27.750000" style="fill:rgb(0,0,255);stroke:rgb(0,0,255);stroke-width:0" /> \n  <text x="96.244189" y="60.000000" font-family="inherit" font-size="3.6" fill="rgb(0,0,255)" text-anchor="middle" transform="rotate(-90.000000 96.244189,60.000000)" >705</text> </g>
  Visible = true
  X = 0
  Y = 0
  arrowL1 = 3
  arrowL2 = 1
  arrowW = 2
  arrow_scheme = 0
  autoPlaceOffset = 2
  autoPlaceText = true
  click1_x = 98.2442
  click1_y = 77.2324
  click2_x = 98.2442
  click2_y = 77.2324
  comma_decimal_place = false
  dimension_line_overshoot = 1
  gap_datum_points = 2
  halfDimension_linear = false
  lineColor = rgb(0,0,255)
  strokeWidth = 0.5
  textFormat_linear = %(value)3.3f
  textRenderer_color = rgb(0,0,255)
  textRenderer_family = inherit
  textRenderer_size = 3.6
  unit_custom_scale = 1
  unit_scheme = 0
FEATURE [Drawing::FeatureViewPython] text006  # drawing view (typed FeaturePython)
  Rotation = 0
  ViewResult = <g> <text x="60.000000" y="90.000000" font-family="inherit" font-size="5" fill="rgb(0,0,0)" text-anchor="inherit" transform="rotate(270.000000 60.000000,90.000000)" >Abdeckung vorne unten</text> </g>
  Visible = true
  X = 0
  Y = 0
  click1_x = 60
  click1_y = 90
  rotation = 270
  text = Abdeckung vorne unten
  textRenderer_addText_color = rgb(0,0,0)
  textRenderer_addText_family = inherit
  textRenderer_addText_size = 5
FEATURE [Drawing::FeatureViewPart] Ortho006  label="Ortho_0_006"
  Direction = (0,1,0)
  HiddenWidth = 0.15
  LineWidth = 0.35
  Rotation = 90
  Scale = 0.1
  ShowHiddenLines = false
  ShowSmoothLines = false
  Source = -> Box006
  Tolerance = 0.05
  ViewResult = <g id="Ortho_0_006"\n   transform="rotate(90,110,24.75) translate(110,24.75) scale(0.1,0.1)"\n  >\n<g   fill="none"\n   stroke="rgb(0, 0, 0)"\n   stroke-linecap="butt"\n   stroke-linejoin="miter"\n   stroke-width="3.500000"\n   transform="scale(1,-1)"\n  >\n<path id= "1" d=" M 0 -19 L 705 -19 " />\n<path id= "2" d=" M 0 200 L 705 200 " />\n<path id= "3" d=" M 0 -19 L 0 200 " />\n<path id= "4" d=" M 705 -19 L 705 200 " />\n</g>\n</g>
  Visible = true
  X = 110
  Y = 24.75
FEATURE [Drawing::FeatureViewPython] text007  # drawing view (typed FeaturePython)
  Rotation = 0
  ViewResult = <g> <text x="120.000000" y="70.000000" font-family="inherit" font-size="5" fill="rgb(0,0,0)" text-anchor="inherit" transform="rotate(270.000000 120.000000,70.000000)" >Türe</text> </g>
  Visible = true
  X = 0
  Y = 0
  click1_x = 120
  click1_y = 70
  rotation = 270
  text = Türe
  textRenderer_addText_color = rgb(0,0,0)
  textRenderer_addText_family = inherit
  textRenderer_addText_size = 5
FEATURE [Drawing::FeatureViewPart] Ortho007  label="Ortho_0_007"
  Direction = (1,0,0)
  HiddenWidth = 0.15
  LineWidth = 0.35
  Rotation = -90
  Scale = 0.1
  ShowHiddenLines = false
  ShowSmoothLines = false
  Source = -> Box007
  Tolerance = 0.05
  ViewResult = <g id="Ortho_0_007"\n   transform="rotate(-90,35,190.95) translate(35,190.95) scale(0.1,0.1)"\n  >\n<g   fill="none"\n   stroke="rgb(0, 0, 0)"\n   stroke-linecap="butt"\n   stroke-linejoin="miter"\n   stroke-width="3.500000"\n   transform="scale(1,-1)"\n  >\n<path id= "1" d=" M 19 0 L 700 0 " />\n<path id= "2" d=" M 700 0 L 700 -300 " />\n<path id= "3" d=" M 19 -300 L 700 -300 " />\n<path id= "4" d=" M 19 0 L 19 -300 " />\n</g>\n</g>
  Visible = true
  X = 35
  Y = 190.95
FEATURE [Drawing::FeatureViewPython] dim015  # drawing view (typed FeaturePython)
  Rotation = 0
  ViewResult = <g> \n  <line x1="35.000000" y1="191.050000" x2="35.000000" y2="200.895690" style="stroke:rgb(0,0,255);stroke-width:0.50" />\n<line x1="65.000000" y1="191.050000" x2="65.000000" y2="200.895690" style="stroke:rgb(0,0,255);stroke-width:0.50" />\n<line x1="35.000000" y1="199.895690" x2="65.000000" y2="199.895690" style="stroke:rgb(0,0,255);stroke-width:0.50" /> \n  <polygon points="65.000000,199.895690 62.000000,198.895690 61.000000,199.895690 62.000000,200.895690" style="fill:rgb(0,0,255);stroke:rgb(0,0,255);stroke-width:0" /><polygon points="35.000000,199.895690 38.000000,200.895690 39.000000,199.895690 38.000000,198.895690" style="fill:rgb(0,0,255);stroke:rgb(0,0,255);stroke-width:0" /> \n  <text x="50.000000" y="197.895690" font-family="inherit" font-size="3.6" fill="rgb(0,0,255)" text-anchor="middle" transform="rotate(0.000000 50.000000,197.895690)" >300</text> </g>
  Visible = true
  X = 0
  Y = 0
  arrowL1 = 3
  arrowL2 = 1
  arrowW = 2
  arrow_scheme = 0
  autoPlaceOffset = 2
  autoPlaceText = true
  click1_x = 48.2703
  click1_y = 199.896
  click2_x = 48.2703
  click2_y = 199.896
  comma_decimal_place = false
  dimension_line_overshoot = 1
  gap_datum_points = 2
  halfDimension_linear = false
  lineColor = rgb(0,0,255)
  strokeWidth = 0.5
  textFormat_linear = %(value)3.3f
  textRenderer_color = rgb(0,0,255)
  textRenderer_family = inherit
  textRenderer_size = 3.6
  unit_custom_scale = 1
  unit_scheme = 0
FEATURE [Drawing::FeatureViewPython] dim016  # drawing view (typed FeaturePython)
  Rotation = 0
  ViewResult = <g> \n  <line x1="67.000000" y1="189.050000" x2="75.960884" y2="189.050000" style="stroke:rgb(0,0,255);stroke-width:0.50" />\n<line x1="67.000000" y1="120.950000" x2="75.960884" y2="120.950000" style="stroke:rgb(0,0,255);stroke-width:0.50" />\n<line x1="74.960884" y1="189.050000" x2="74.960884" y2="120.950000" style="stroke:rgb(0,0,255);stroke-width:0.50" /> \n  <polygon points="74.960884,120.950000 73.960884,123.950000 74.960884,124.950000 75.960884,123.950000" style="fill:rgb(0,0,255);stroke:rgb(0,0,255);stroke-width:0" /><polygon points="74.960884,189.050000 75.960884,186.050000 74.960884,185.050000 73.960884,186.050000" style="fill:rgb(0,0,255);stroke:rgb(0,0,255);stroke-width:0" /> \n  <text x="72.960884" y="155.000000" font-family="inherit" font-size="3.6" fill="rgb(0,0,255)" text-anchor="middle" transform="rotate(-90.000000 72.960884,155.000000)" >681</text> </g>
  Visible = true
  X = 0
  Y = 0
  arrowL1 = 3
  arrowL2 = 1
  arrowW = 2
  arrow_scheme = 0
  autoPlaceOffset = 2
  autoPlaceText = true
  click1_x = 74.9609
  click1_y = 162.983
  click2_x = 74.9609
  click2_y = 162.983
  comma_decimal_place = false
  dimension_line_overshoot = 1
  gap_datum_points = 2
  halfDimension_linear = false
  lineColor = rgb(0,0,255)
  strokeWidth = 0.5
  textFormat_linear = %(value)3.3f
  textRenderer_color = rgb(0,0,255)
  textRenderer_family = inherit
  textRenderer_size = 3.6
  unit_custom_scale = 1
  unit_scheme = 0
FEATURE [Drawing::FeatureViewPython] text008  # drawing view (typed FeaturePython)
  Rotation = 0
  ViewResult = <g> <text x="51.000000" y="183.000000" font-family="inherit" font-size="5" fill="rgb(0,0,0)" text-anchor="inherit" transform="rotate(270.000000 51.000000,183.000000)" >Stütze mitte (Trennwand)</text> </g>
  Visible = true
  X = 0
  Y = 0
  click1_x = 51
  click1_y = 183
  rotation = 270
  text = Stütze mitte (Trennwand)
  textRenderer_addText_color = rgb(0,0,0)
  textRenderer_addText_family = inherit
  textRenderer_addText_size = 5
FEATURE [Drawing::FeatureViewPart] Ortho008  label="Ortho_0_008"
  Direction = (0,1,0)
  HiddenWidth = 0.15
  LineWidth = 0.35
  Rotation = 90
  Scale = 0.1
  ShowHiddenLines = false
  ShowSmoothLines = false
  Source = -> Box008
  Tolerance = 0.05
  ViewResult = <g id="Ortho_0_008"\n   transform="rotate(90,93.45,49.75) translate(93.45,49.75) scale(0.1,0.1)"\n  >\n<g   fill="none"\n   stroke="rgb(0, 0, 0)"\n   stroke-linecap="butt"\n   stroke-linejoin="miter"\n   stroke-width="3.500000"\n   transform="scale(1,-1)"\n  >\n<path id= "1" d=" M 705 -19 L 1300 -19 " />\n<path id= "2" d=" M 705 750 L 1300 750 " />\n<path id= "3" d=" M 705 -19 L 705 750 " />\n<path id= "4" d=" M 1300 -19 L 1300 750 " />\n</g>\n</g>
  Visible = true
  X = 93.45
  Y = 49.75
FEATURE [Drawing::FeatureViewPython] dim017  # drawing view (typed FeaturePython)
  Rotation = 0
  ViewResult = <g> \n  <line x1="91.550000" y1="181.750000" x2="91.550000" y2="191.241637" style="stroke:rgb(0,0,255);stroke-width:0.50" />\n<line x1="168.450000" y1="181.750000" x2="168.450000" y2="191.241637" style="stroke:rgb(0,0,255);stroke-width:0.50" />\n<line x1="91.550000" y1="190.241637" x2="168.450000" y2="190.241637" style="stroke:rgb(0,0,255);stroke-width:0.50" /> \n  <polygon points="168.450000,190.241637 165.450000,189.241637 164.450000,190.241637 165.450000,191.241637" style="fill:rgb(0,0,255);stroke:rgb(0,0,255);stroke-width:0" /><polygon points="91.550000,190.241637 94.550000,191.241637 95.550000,190.241637 94.550000,189.241637" style="fill:rgb(0,0,255);stroke:rgb(0,0,255);stroke-width:0" /> \n  <text x="130.000000" y="188.241637" font-family="inherit" font-size="3.6" fill="rgb(0,0,255)" text-anchor="middle" transform="rotate(0.000000 130.000000,188.241637)" >769</text> </g>
  Visible = true
  X = 0
  Y = 0
  arrowL1 = 3
  arrowL2 = 1
  arrowW = 2
  arrow_scheme = 0
  autoPlaceOffset = 2
  autoPlaceText = true
  click1_x = 128.342
  click1_y = 190.242
  click2_x = 128.342
  click2_y = 190.242
  comma_decimal_place = false
  dimension_line_overshoot = 1
  gap_datum_points = 2
  halfDimension_linear = false
  lineColor = rgb(0,0,255)
  strokeWidth = 0.5
  textFormat_linear = %(value)3.3f
  textRenderer_color = rgb(0,0,255)
  textRenderer_family = inherit
  textRenderer_size = 3.6
  unit_custom_scale = 1
  unit_scheme = 0
FEATURE [Drawing::FeatureViewPython] dim018  # drawing view (typed FeaturePython)
  Rotation = 0
  ViewResult = <g> \n  <line x1="170.450000" y1="120.250000" x2="177.612385" y2="120.250000" style="stroke:rgb(0,0,255);stroke-width:0.50" />\n<line x1="170.450000" y1="179.750000" x2="177.612385" y2="179.750000" style="stroke:rgb(0,0,255);stroke-width:0.50" />\n<line x1="176.612385" y1="120.250000" x2="176.612385" y2="179.750000" style="stroke:rgb(0,0,255);stroke-width:0.50" /> \n  <polygon points="176.612385,179.750000 177.612385,176.750000 176.612385,175.750000 175.612385,176.750000" style="fill:rgb(0,0,255);stroke:rgb(0,0,255);stroke-width:0" /><polygon points="176.612385,120.250000 175.612385,123.250000 176.612385,124.250000 177.612385,123.250000" style="fill:rgb(0,0,255);stroke:rgb(0,0,255);stroke-width:0" /> \n  <text x="174.612385" y="150.000000" font-family="inherit" font-size="3.6" fill="rgb(0,0,255)" text-anchor="middle" transform="rotate(-90.000000 174.612385,150.000000)" >595</text> </g>
  Visible = true
  X = 0
  Y = 0
  arrowL1 = 3
  arrowL2 = 1
  arrowW = 2
  arrow_scheme = 0
  autoPlaceOffset = 2
  autoPlaceText = true
  click1_x = 176.612
  click1_y = 155.601
  click2_x = 176.612
  click2_y = 155.601
  comma_decimal_place = false
  dimension_line_overshoot = 1
  gap_datum_points = 2
  halfDimension_linear = false
  lineColor = rgb(0,0,255)
  strokeWidth = 0.5
  textFormat_linear = %(value)3.3f
  textRenderer_color = rgb(0,0,255)
  textRenderer_family = inherit
  textRenderer_size = 3.6
  unit_custom_scale = 1
  unit_scheme = 0
FEATURE [Drawing::FeatureViewPython] text009  # drawing view (typed FeaturePython)
  Rotation = 0
  ViewResult = <g> <text x="115.000000" y="150.000000" font-family="inherit" font-size="5" fill="rgb(0,0,0)" text-anchor="inherit" transform="rotate(0.000000 115.000000,150.000000)" >Klappe oben</text> </g>
  Visible = true
  X = 0
  Y = 0
  click1_x = 115
  click1_y = 150
  rotation = 0
  text = Klappe oben
  textRenderer_addText_color = rgb(0,0,0)
  textRenderer_addText_family = inherit
  textRenderer_addText_size = 5
FEATURE [Drawing::FeatureViewPart] Ortho009  label="Ortho_0_009"
  Direction = (0,1,0)
  HiddenWidth = 0.15
  LineWidth = 0.35
  Rotation = 90
  Scale = 0.1
  ShowHiddenLines = false
  ShowSmoothLines = false
  Source = -> Box009
  Tolerance = 0.05
  ViewResult = <g id="Ortho_0_009"\n   transform="rotate(90,100,24.05) translate(100,24.05) scale(0.1,0.1)"\n  >\n<g   fill="none"\n   stroke="rgb(0, 0, 0)"\n   stroke-linecap="butt"\n   stroke-linejoin="miter"\n   stroke-width="3.500000"\n   transform="scale(1,-1)"\n  >\n<path id= "1" d=" M 19 650 L 700 650 " />\n<path id= "2" d=" M 19 750 L 700 750 " />\n<path id= "3" d=" M 19 650 L 19 750 " />\n<path id= "4" d=" M 700 650 L 700 750 " />\n</g>\n</g>
  Visible = true
  X = 100
  Y = 24.05
FEATURE [Drawing::FeatureViewPython] dim013  # drawing view (typed FeaturePython)
  Rotation = 0
  ViewResult = <g> \n  <line x1="132.000000" y1="24.750000" x2="141.267714" y2="24.750000" style="stroke:rgb(0,0,255);stroke-width:0.50" />\n<line x1="132.000000" y1="95.250000" x2="141.267714" y2="95.250000" style="stroke:rgb(0,0,255);stroke-width:0.50" />\n<line x1="140.267714" y1="24.750000" x2="140.267714" y2="95.250000" style="stroke:rgb(0,0,255);stroke-width:0.50" /> \n  <polygon points="140.267714,95.250000 141.267714,92.250000 140.267714,91.250000 139.267714,92.250000" style="fill:rgb(0,0,255);stroke:rgb(0,0,255);stroke-width:0" /><polygon points="140.267714,24.750000 139.267714,27.750000 140.267714,28.750000 141.267714,27.750000" style="fill:rgb(0,0,255);stroke:rgb(0,0,255);stroke-width:0" /> \n  <text x="138.267714" y="60.000000" font-family="inherit" font-size="3.6" fill="rgb(0,0,255)" text-anchor="middle" transform="rotate(-90.000000 138.267714,60.000000)" >705</text> </g>
  Visible = true
  X = 0
  Y = 0
  arrowL1 = 3
  arrowL2 = 1
  arrowW = 2
  arrow_scheme = 0
  autoPlaceOffset = 2
  autoPlaceText = true
  click1_x = 140.268
  click1_y = 55.0849
  click2_x = 140.268
  click2_y = 55.0849
  comma_decimal_place = false
  dimension_line_overshoot = 1
  gap_datum_points = 2
  halfDimension_linear = false
  lineColor = rgb(0,0,255)
  strokeWidth = 0.5
  textFormat_linear = %(value)3.3f
  textRenderer_color = rgb(0,0,255)
  textRenderer_family = inherit
  textRenderer_size = 3.6
  unit_custom_scale = 1
  unit_scheme = 0
FEATURE [Drawing::FeatureViewPython] dim014  # drawing view (typed FeaturePython)
  Rotation = 0
  ViewResult = <g> \n  <line x1="108.100000" y1="97.250000" x2="108.100000" y2="106.058814" style="stroke:rgb(0,0,255);stroke-width:0.50" />\n<line x1="130.000000" y1="97.250000" x2="130.000000" y2="106.058814" style="stroke:rgb(0,0,255);stroke-width:0.50" />\n<line x1="108.100000" y1="105.058814" x2="130.000000" y2="105.058814" style="stroke:rgb(0,0,255);stroke-width:0.50" /> \n  <polygon points="130.000000,105.058814 127.000000,104.058814 126.000000,105.058814 127.000000,106.058814" style="fill:rgb(0,0,255);stroke:rgb(0,0,255);stroke-width:0" /><polygon points="108.100000,105.058814 111.100000,106.058814 112.100000,105.058814 111.100000,104.058814" style="fill:rgb(0,0,255);stroke:rgb(0,0,255);stroke-width:0" /> \n  <text x="119.050000" y="103.058814" font-family="inherit" font-size="3.6" fill="rgb(0,0,255)" text-anchor="middle" transform="rotate(0.000000 119.050000,103.058814)" >219</text> </g>
  Visible = true
  X = 0
  Y = 0
  arrowL1 = 3
  arrowL2 = 1
  arrowW = 2
  arrow_scheme = 0
  autoPlaceOffset = 2
  autoPlaceText = true
  click1_x = 120.392
  click1_y = 105.059
  click2_x = 120.392
  click2_y = 105.059
  comma_decimal_place = false
  dimension_line_overshoot = 1
  gap_datum_points = 2
  halfDimension_linear = false
  lineColor = rgb(0,0,255)
  strokeWidth = 0.5
  textFormat_linear = %(value)3.3f
  textRenderer_color = rgb(0,0,255)
  textRenderer_family = inherit
  textRenderer_size = 3.6
  unit_custom_scale = 1
  unit_scheme = 0
FEATURE [Drawing::FeatureViewPython] dim019  # drawing view (typed FeaturePython)
  Rotation = 0
  ViewResult = <g> \n  <line x1="155.000000" y1="96.050000" x2="155.000000" y2="106.058814" style="stroke:rgb(0,0,255);stroke-width:0.50" />\n<line x1="175.000000" y1="96.050000" x2="175.000000" y2="106.058814" style="stroke:rgb(0,0,255);stroke-width:0.50" />\n<line x1="155.000000" y1="105.058814" x2="175.000000" y2="105.058814" style="stroke:rgb(0,0,255);stroke-width:0.50" /> \n  <polygon points="175.000000,105.058814 172.000000,104.058814 171.000000,105.058814 172.000000,106.058814" style="fill:rgb(0,0,255);stroke:rgb(0,0,255);stroke-width:0" /><polygon points="155.000000,105.058814 158.000000,106.058814 159.000000,105.058814 158.000000,104.058814" style="fill:rgb(0,0,255);stroke:rgb(0,0,255);stroke-width:0" /> \n  <text x="165.000000" y="103.058814" font-family="inherit" font-size="3.6" fill="rgb(0,0,255)" text-anchor="middle" transform="rotate(0.000000 165.000000,103.058814)" >200</text> </g>
  Visible = true
  X = 0
  Y = 0
  arrowL1 = 3
  arrowL2 = 1
  arrowW = 2
  arrow_scheme = 0
  autoPlaceOffset = 2
  autoPlaceText = true
  click1_x = 162.983
  click1_y = 105.059
  click2_x = 162.983
  click2_y = 105.059
  comma_decimal_place = false
  dimension_line_overshoot = 1
  gap_datum_points = 2
  halfDimension_linear = false
  lineColor = rgb(0,0,255)
  strokeWidth = 0.5
  textFormat_linear = %(value)3.3f
  textRenderer_color = rgb(0,0,255)
  textRenderer_family = inherit
  textRenderer_size = 3.6
  unit_custom_scale = 1
  unit_scheme = 0
FEATURE [Drawing::FeatureViewPython] dim020  # drawing view (typed FeaturePython)
  Rotation = 0
  ViewResult = <g> \n  <line x1="177.000000" y1="25.950000" x2="186.698553" y2="25.950000" style="stroke:rgb(0,0,255);stroke-width:0.50" />\n<line x1="177.000000" y1="94.050000" x2="186.698553" y2="94.050000" style="stroke:rgb(0,0,255);stroke-width:0.50" />\n<line x1="185.698553" y1="25.950000" x2="185.698553" y2="94.050000" style="stroke:rgb(0,0,255);stroke-width:0.50" /> \n  <polygon points="185.698553,94.050000 186.698553,91.050000 185.698553,90.050000 184.698553,91.050000" style="fill:rgb(0,0,255);stroke:rgb(0,0,255);stroke-width:0" /><polygon points="185.698553,25.950000 184.698553,28.950000 185.698553,29.950000 186.698553,28.950000" style="fill:rgb(0,0,255);stroke:rgb(0,0,255);stroke-width:0" /> \n  <text x="183.698553" y="60.000000" font-family="inherit" font-size="3.6" fill="rgb(0,0,255)" text-anchor="middle" transform="rotate(-90.000000 183.698553,60.000000)" >681</text> </g>
  Visible = true
  X = 0
  Y = 0
  arrowL1 = 3
  arrowL2 = 1
  arrowW = 2
  arrow_scheme = 0
  autoPlaceOffset = 2
  autoPlaceText = true
  click1_x = 185.699
  click1_y = 70.9857
  click2_x = 185.699
  click2_y = 70.9857
  comma_decimal_place = false
  dimension_line_overshoot = 1
  gap_datum_points = 2
  halfDimension_linear = false
  lineColor = rgb(0,0,255)
  strokeWidth = 0.5
  textFormat_linear = %(value)3.3f
  textRenderer_color = rgb(0,0,255)
  textRenderer_family = inherit
  textRenderer_size = 3.6
  unit_custom_scale = 1
  unit_scheme = 0
FEATURE [Drawing::FeatureViewPython] text010  # drawing view (typed FeaturePython)
  Rotation = 0
  ViewResult = <g> <text x="167.000000" y="80.639739" font-family="inherit" font-size="5" fill="rgb(0,0,0)" text-anchor="inherit" transform="rotate(270.000000 167.000000,80.639739)" >Stütze hinten</text> </g>
  Visible = true
  X = 0
  Y = 0
  click1_x = 167
  click1_y = 80.6397
  rotation = 270
  text = Stütze hinten
  textRenderer_addText_color = rgb(0,0,0)
  textRenderer_addText_family = inherit
  textRenderer_addText_size = 5
FEATURE [Drawing::FeaturePage] Page001  label="Front"
  EditableTexts = Manuel Dillmann | PC-Schrank | Front | Stütze mitte | Stütze hinten | A4 | 2 / X | 0.1 | ... | ... | 17/04/2019 | REV A
  Group = -> [Ortho005,dim011,dim012,text006,Ortho006,text007,Ortho007,dim015,dim016,text008,Ortho008,dim017,dim018,text009,Ortho009,dim013,dim014,dim019,dim020,text010]
  Template = C:/Program Files/FreeCAD 0.17/data/Mod/Drawing/Templates/A4_Portrait_ISO7200.svg
FEATURE [Part::FeaturePython] Connect  # WARN: FeaturePython — macro-defined, semantics opaque (R4)
  Objects = -> [Box010,Box011,Box012,Box013,Box014,Box015,Box016,Box017,Box018,Box019,Cylinder002,Cylinder003]
  Tolerance = 0
FEATURE [Drawing::FeatureViewPart] View  label="Vo"
  Direction = (0,-1,0)
  HiddenWidth = 0.15
  LineWidth = 0.35
  Rotation = 90
  Scale = 0.07
  ShowHiddenLines = false
  ShowSmoothLines = false
  Source = -> Connect
  Tolerance = 0.05
  ViewResult = <g id="Vo"\n   transform="rotate(90,35,105) translate(35,105) scale(0.07,0.07)"\n  >\n<g   fill="none"\n   stroke="rgb(0, 0, 0)"\n   stroke-linecap="butt"\n   stroke-linejoin="miter"\n   stroke-width="5.000000"\n   transform="scale(1,-1)"\n  >\n<path id= "1" d=" M -705 750 L -1300 750 " />\n<circle cx ="-600" cy ="160" r ="10" /><path id= "3" d=" M 0 -19 L 0 200 " />\n<path id= "4" d=" M 0 -19 L -705 -19 " />\n<path id= "5" d=" M 0 200 L -705 200 " />\n<path id= "6" d=" M -705 -19 L -705 200 " />\n<circle cx ="-1200" cy ="380" r ="10" /><path id= "8" d=" M -705 -19 L -1300 -19 " />\n<path id= "9" d=" M -705 200 L -705 750 " />\n<path id= "10" d=" M -1300 -19 L -1300 750 " />\n<path id= "11" d=" M 0 200 L 0 750 " />\n<path id= "12" d=" M 0 750 L -705 750 " />\n</g>\n</g>
  Visible = true
  X = 35
  Y = 105
FEATURE [Drawing::FeatureViewPart] View001  label="Hi"
  Direction = (0,1,0)
  HiddenWidth = 0.15
  LineWidth = 0.35
  Rotation = 270
  Scale = 0.07
  ShowHiddenLines = false
  ShowSmoothLines = false
  Source = -> Connect
  Tolerance = 0.05
  ViewResult = <g id="Hi"\n   transform="rotate(270,85,210) translate(85,210) scale(0.07,0.07)"\n  >\n<g   fill="none"\n   stroke="rgb(0, 0, 0)"\n   stroke-linecap="butt"\n   stroke-linejoin="miter"\n   stroke-width="5.000000"\n   transform="scale(1,-1)"\n  >\n<path id= "1" d=" M 0 0 L 0 750 " />\n<path id= "2" d=" M 19 190 L 700 190 " />\n<path id= "3" d=" M 1281 0 L 1281 731 " />\n<path id= "4" d=" M 700 750 L 1300 750 " />\n<path id= "5" d=" M 700 0 L 700 190 " />\n<path id= "6" d=" M 0 -19 L 0 0 " />\n<path id= "7" d=" M 0 -19 L 1300 -19 " />\n<path id= "8" d=" M 0 0 L 19 0 " />\n<path id= "9" d=" M 1300 -19 L 1300 0 " />\n<path id= "10" d=" M 19 0 L 700 0 " />\n<path id= "11" d=" M 1281 0 L 1300 0 " />\n<path id= "12" d=" M 700 0 L 719 0 " />\n<path id= "13" d=" M 719 0 L 1281 0 " />\n<path id= "14" d=" M 700 731 L 700 750 " />\n<path id= "15" d=" M 700 731 L 719 731 " />\n<path id= "16" d=" M 719 731 L 1281 731 " />\n<path id= "17" d=" M 1300 731 L 1300 750 " />\n<path id= "18" d=" M 1281 731 L 1300 731 " />\n<path id= "19" d=" M 700 209 L 700 650 " />\n<path id= "20" d=" M 19 190 L 19 209 " />\n<path id= "21" d=" M 19 209 L 700 209 " />\n<path id= "22" d=" M 700 190 L 700 209 " />\n<path id= "23" d=" M 0 750 L 19 750 " />\n<path id= "24" d=" M 19 0 L 19 190 " />\n<path id= "25" d=" M 19 650 L 19 750 " />\n<path id= "26" d=" M 19 209 L 19 650 " />\n<path id= "27" d=" M 19 750 L 700 750 " />\n<path id= "28" d=" M 719 0 L 719 731 " />\n<path id= "29" d=" M 1300 0 L 1300 731 " />\n<path id= "30" d=" M 19 650 L 700 650 " />\n<path id= "31" d=" M 700 650 L 700 731 " />\n</g>\n</g>
  Visible = true
  X = 85
  Y = 210
FEATURE [Drawing::FeatureViewPart] View002  label="Li"
  Direction = (-1,0,0)
  HiddenWidth = 0.15
  LineWidth = 0.35
  Rotation = 90
  Scale = 0.07
  ShowHiddenLines = false
  ShowSmoothLines = false
  Source = -> Connect
  Tolerance = 0.05
  ViewResult = <g id="Li"\n   transform="rotate(90,150,106) translate(150,106) scale(0.07,0.07)"\n  >\n<g   fill="none"\n   stroke="rgb(0, 0, 0)"\n   stroke-linecap="butt"\n   stroke-linejoin="miter"\n   stroke-width="5.000000"\n   transform="scale(1,-1)"\n  >\n<path id= "1" d=" M -590 19 L -590 39 " />\n<path id= "2" d=" M -610 19 L -610 39 " />\n<path id= "3" d=" M -1190 19 L -1190 39 " />\n<path id= "4" d=" M -1210 19 L -1210 39 " />\n</g>\n<g   fill="none"\n   stroke="rgb(0, 0, 0)"\n   stroke-linecap="butt"\n   stroke-linejoin="miter"\n   stroke-width="5.000000"\n   transform="scale(1,-1)"\n  >\n<path d="M-610,39 L-609.749,39  L-609.01,39  L-607.818,39  L-606.235,39  L-604.339,39  L-602.225,39  L-600,39  L-597.775,39  L-595.661,39  L-593.765,39  L-592.182,39  L-590.99,39  L-590.251,39  L-590,39 " /><path id= "2" d=" M 0 -300 L -1300 -300 " />\n<path id= "3" d=" M 0 0 L 0 -300 " />\n<path id= "4" d=" M 0 19 L -705 19 " />\n<path d="M-1210,39 L-1209.75,39  L-1209.01,39  L-1207.82,39  L-1206.23,39  L-1204.34,39  L-1202.23,39  L-1200,39  L-1197.77,39  L-1195.66,39  L-1193.77,39  L-1192.18,39  L-1190.99,39  L-1190.25,39  L-1190,39 " /><path id= "6" d=" M -1300 0 L -1300 -300 " />\n<path id= "7" d=" M -705 19 L -1300 19 " />\n<path id= "8" d=" M -705 19 L -705 0 " />\n<path id= "9" d=" M -1300 19 L -1300 0 " />\n<path id= "10" d=" M -705 0 L -1300 0 " />\n<path id= "11" d=" M 0 19 L 0 0 " />\n<path id= "12" d=" M 0 0 L -705 0 " />\n</g>\n</g>
  Visible = true
  X = 150
  Y = 106
FEATURE [Drawing::FeatureViewPart] View003  label="Re"
  Direction = (1,0,0)
  HiddenWidth = 0.15
  LineWidth = 0.35
  Rotation = 270
  Scale = 0.07
  ShowHiddenLines = false
  ShowSmoothLines = false
  Source = -> Connect
  Tolerance = 0.05
  ViewResult = <blob: 2151 chars omitted>
  Visible = true
  X = 130
  Y = 210
FEATURE [Drawing::FeatureViewPart] View004  label="VR"
  Direction = (1,-1,1)
  HiddenWidth = 0.15
  LineWidth = 0.35
  Rotation = 60
  Scale = 0.06
  ShowHiddenLines = false
  ShowSmoothLines = false
  Source = -> Connect
  Tolerance = 0.05
  ViewResult = <blob: 3728 chars omitted>
  Visible = true
  X = 40
  Y = 90
FEATURE [Drawing::FeatureViewPython] dimStack001  # drawing view (typed FeaturePython)
  Rotation = 0
  ViewResult = <g> <line x1="33.670000" y1="90.143943" x2="49.000000" y2="90.143943" style="stroke:rgb(0,0,255);stroke-width:0.50" />\n<polygon points="33.670000,90.143943 36.670000,91.143943 37.670000,90.143943 36.670000,89.143943" style="fill:rgb(0,0,255);stroke:rgb(0,0,255);stroke-width:0" />\n<polygon points="49.000000,90.143943 46.000000,89.143943 45.000000,90.143943 46.000000,91.143943" style="fill:rgb(0,0,255);stroke:rgb(0,0,255);stroke-width:0" />\n<text x="41.335000" y="88.143943" font-family="inherit" font-size="3.6" fill="rgb(0,0,255)" text-anchor="middle" transform="rotate(0.000000 41.335000,88.143943)" >219</text> </g> \n<g> <line x1="33.670000" y1="83.143943" x2="87.500000" y2="83.143943" style="stroke:rgb(0,0,255);stroke-width:0.50" />\n<polygon points="33.670000,83.143943 36.670000,84.143943 37.670000,83.143943 36.670000,82.143943" style="fill:rgb(0,0,255);stroke:rgb(0,0,255);stroke-width:0" />\n<polygon points="87.500000,83.143943 84.500000,82.143943 83.500000,83.143943 84.500000,84.143943" style="fill:rgb(0,0,255);stroke:rgb(0,0,255);stroke-width:0" />\n<text x="60.585000" y="81.143943" font-family="inherit" font-size="3.6" fill="rgb(0,0,255)" text-anchor="middle" transform="rotate(0.000000 60.585000,81.143943)" >769</text> </g> 
  Visible = true
  X = 0
  Y = 0
  arrowL1 = 3
  arrowL2 = 1
  arrowW = 2
  arrow_scheme = 0
  autoPlaceOffset = 2
  click1_x = 73.3585
  click1_y = 90.1439
  comma_decimal_place = false
  dimension_line_overshoot = 1
  gap_datum_points = 2
  lineColor = rgb(0,0,255)
  stack_offset = 7
  stack_offset0 = 0
  strokeWidth = 0.5
  textFormat_linear = %(value)3.3f
  textRenderer_color = rgb(0,0,255)
  textRenderer_family = inherit
  textRenderer_size = 3.6
  unit_custom_scale = 1
  unit_scheme = 0
FEATURE [Drawing::FeatureViewPython] dimStack002  # drawing view (typed FeaturePython)
  Rotation = 0
  ViewResult = <g> <line x1="65.898330" y1="14.000000" x2="65.898330" y2="55.650000" style="stroke:rgb(0,0,255);stroke-width:0.50" />\n<polygon points="65.898330,14.000000 64.898330,17.000000 65.898330,18.000000 66.898330,17.000000" style="fill:rgb(0,0,255);stroke:rgb(0,0,255);stroke-width:0" />\n<polygon points="65.898330,55.650000 66.898330,52.650000 65.898330,51.650000 64.898330,52.650000" style="fill:rgb(0,0,255);stroke:rgb(0,0,255);stroke-width:0" />\n<text x="63.898330" y="34.825000" font-family="inherit" font-size="3.6" fill="rgb(0,0,255)" text-anchor="middle" transform="rotate(-90.000000 63.898330,34.825000)" >595</text> </g> \n<g> <line x1="72.898330" y1="14.000000" x2="72.898330" y2="105.000000" style="stroke:rgb(0,0,255);stroke-width:0.50" />\n<polygon points="72.898330,14.000000 71.898330,17.000000 72.898330,18.000000 73.898330,17.000000" style="fill:rgb(0,0,255);stroke:rgb(0,0,255);stroke-width:0" />\n<polygon points="72.898330,105.000000 73.898330,102.000000 72.898330,101.000000 71.898330,102.000000" style="fill:rgb(0,0,255);stroke:rgb(0,0,255);stroke-width:0" />\n<text x="70.898330" y="59.500000" font-family="inherit" font-size="3.6" fill="rgb(0,0,255)" text-anchor="middle" transform="rotate(-90.000000 70.898330,59.500000)" >1300</text> </g> 
  Visible = true
  X = 0
  Y = 0
  arrowL1 = 3
  arrowL2 = 1
  arrowW = 2
  arrow_scheme = 0
  autoPlaceOffset = 2
  click1_x = 65.8983
  click1_y = 100.091
  comma_decimal_place = false
  dimension_line_overshoot = 1
  gap_datum_points = 2
  lineColor = rgb(0,0,255)
  stack_offset = 7
  stack_offset0 = 0
  strokeWidth = 0.5
  textFormat_linear = %(value)3.3f
  textRenderer_color = rgb(0,0,255)
  textRenderer_family = inherit
  textRenderer_size = 3.6
  unit_custom_scale = 1
  unit_scheme = 0
FEATURE [Drawing::FeatureViewPython] dim021  # drawing view (typed FeaturePython)
  Rotation = 0
  ViewResult = <g> \n  <line x1="127.000000" y1="106.000000" x2="118.363014" y2="106.000000" style="stroke:rgb(0,0,255);stroke-width:0.50" />\n<line x1="127.000000" y1="15.000000" x2="118.363014" y2="15.000000" style="stroke:rgb(0,0,255);stroke-width:0.50" />\n<line x1="119.363014" y1="106.000000" x2="119.363014" y2="15.000000" style="stroke:rgb(0,0,255);stroke-width:0.50" /> \n  <polygon points="119.363014,15.000000 118.363014,18.000000 119.363014,19.000000 120.363014,18.000000" style="fill:rgb(0,0,255);stroke:rgb(0,0,255);stroke-width:0" /><polygon points="119.363014,106.000000 120.363014,103.000000 119.363014,102.000000 118.363014,103.000000" style="fill:rgb(0,0,255);stroke:rgb(0,0,255);stroke-width:0" /> \n  <text x="117.363014" y="60.500000" font-family="inherit" font-size="3.6" fill="rgb(0,0,255)" text-anchor="middle" transform="rotate(-90.000000 117.363014,60.500000)" >1300</text> </g>
  Visible = true
  X = 0
  Y = 0
  arrowL1 = 3
  arrowL2 = 1
  arrowW = 2
  arrow_scheme = 0
  autoPlaceOffset = 2
  autoPlaceText = true
  click1_x = 119.363
  click1_y = 88.2789
  click2_x = 119.363
  click2_y = 88.2789
  comma_decimal_place = false
  dimension_line_overshoot = 1
  gap_datum_points = 2
  halfDimension_linear = false
  lineColor = rgb(0,0,255)
  strokeWidth = 0.5
  textFormat_linear = %(value)3.3f
  textRenderer_color = rgb(0,0,255)
  textRenderer_family = inherit
  textRenderer_size = 3.6
  unit_custom_scale = 0.9
  unit_scheme = 0
FEATURE [Drawing::FeatureViewPython] dimStack003  # drawing view (typed FeaturePython)
  Rotation = 0
  ViewResult = <g> <line x1="129.000000" y1="90.143943" x2="150.000000" y2="90.143943" style="stroke:rgb(0,0,255);stroke-width:0.50" />\n<polygon points="129.000000,90.143943 132.000000,91.143943 133.000000,90.143943 132.000000,89.143943" style="fill:rgb(0,0,255);stroke:rgb(0,0,255);stroke-width:0" />\n<polygon points="150.000000,90.143943 147.000000,89.143943 146.000000,90.143943 147.000000,91.143943" style="fill:rgb(0,0,255);stroke:rgb(0,0,255);stroke-width:0" />\n<text x="139.500000" y="88.143943" font-family="inherit" font-size="3.6" fill="rgb(0,0,255)" text-anchor="middle" transform="rotate(0.000000 139.500000,88.143943)" >300</text> </g> \n<g> <line x1="129.000000" y1="83.143943" x2="151.330000" y2="83.143943" style="stroke:rgb(0,0,255);stroke-width:0.50" />\n<polygon points="129.000000,83.143943 132.000000,84.143943 133.000000,83.143943 132.000000,82.143943" style="fill:rgb(0,0,255);stroke:rgb(0,0,255);stroke-width:0" />\n<polygon points="151.330000,83.143943 148.330000,82.143943 147.330000,83.143943 148.330000,84.143943" style="fill:rgb(0,0,255);stroke:rgb(0,0,255);stroke-width:0" />\n<text x="140.165000" y="81.143943" font-family="inherit" font-size="3.6" fill="rgb(0,0,255)" text-anchor="middle" transform="rotate(0.000000 140.165000,81.143943)" >319</text> </g> 
  Visible = true
  X = 0
  Y = 0
  arrowL1 = 3
  arrowL2 = 1
  arrowW = 2
  arrow_scheme = 0
  autoPlaceOffset = 2
  click1_x = 146.717
  click1_y = 90.1439
  comma_decimal_place = false
  dimension_line_overshoot = 1
  gap_datum_points = 2
  lineColor = rgb(0,0,255)
  stack_offset = 7
  stack_offset0 = 0
  strokeWidth = 0.5
  textFormat_linear = %(value)3.3f
  textRenderer_color = rgb(0,0,255)
  textRenderer_family = inherit
  textRenderer_size = 3.6
  unit_custom_scale = 0.9
  unit_scheme = 0
FEATURE [Drawing::FeatureViewPython] dimStack004  # drawing view (typed FeaturePython)
  Rotation = 0
  ViewResult = <blob: 4232 chars omitted>
  Visible = true
  X = 0
  Y = 0
  arrowL1 = 3
  arrowL2 = 1
  arrowW = 2
  arrow_scheme = 0
  autoPlaceOffset = 2
  click1_x = 65.8983
  click1_y = 155.421
  comma_decimal_place = false
  dimension_line_overshoot = 1
  gap_datum_points = 2
  lineColor = rgb(0,0,255)
  stack_offset = 7
  stack_offset0 = 0
  strokeWidth = 0.5
  textFormat_linear = %(value)3.3f
  textRenderer_color = rgb(0,0,255)
  textRenderer_family = inherit
  textRenderer_size = 3.6
  unit_custom_scale = 0.9
  unit_scheme = 0
FEATURE [Drawing::FeatureViewPython] dimStack005  # drawing view (typed FeaturePython)
  Rotation = 0
  ViewResult = <blob: 4409 chars omitted>
  Visible = true
  X = 0
  Y = 0
  arrowL1 = 3
  arrowL2 = 1
  arrowW = 2
  arrow_scheme = 0
  autoPlaceOffset = 2
  click1_x = 94.8369
  click1_y = 203.303
  comma_decimal_place = false
  dimension_line_overshoot = 1
  gap_datum_points = 2
  lineColor = rgb(0,0,255)
  stack_offset = 7
  stack_offset0 = 0
  strokeWidth = 0.5
  textFormat_linear = %(value)3.3f
  textRenderer_color = rgb(0,0,255)
  textRenderer_family = inherit
  textRenderer_size = 3.6
  unit_custom_scale = 0.9
  unit_scheme = 0
FEATURE [Drawing::FeatureViewPython] dimStack006  # drawing view (typed FeaturePython)
  Rotation = 0
  ViewResult = <blob: 2662 chars omitted>
  Visible = true
  X = 0
  Y = 0
  arrowL1 = 3
  arrowL2 = 1
  arrowW = 2
  arrow_scheme = 0
  autoPlaceOffset = 2
  click1_x = 167.526
  click1_y = 205.575
  comma_decimal_place = false
  dimension_line_overshoot = 1
  gap_datum_points = 2
  lineColor = rgb(0,0,255)
  stack_offset = 7
  stack_offset0 = 0
  strokeWidth = 0.5
  textFormat_linear = %(value)3.3f
  textRenderer_color = rgb(0,0,255)
  textRenderer_family = inherit
  textRenderer_size = 3.6
  unit_custom_scale = 0.9
  unit_scheme = 0
FEATURE [Drawing::FeaturePage] Page002  label="Gesamt"
  EditableTexts = Manuel Dillmann | PC-Schrank | Gesamtansichten | A4 | 3 / X | 0.07 | ... | ... | 17/04/2019 | REV A
  Group = -> [View,View001,View002,View003,dimStack001,dimStack002,dim021,dimStack003,dimStack004,dimStack005,dimStack006]
  Template = C:/Program Files/FreeCAD 0.17/data/Mod/Drawing/Templates/A4_Portrait_ISO7200.svg
FEATURE [Drawing::FeatureViewPart] View005  label="VL"
  Direction = (-1,-1,1)
  HiddenWidth = 0.15
  LineWidth = 0.35
  Rotation = 300
  Scale = 0.06
  ShowHiddenLines = false
  ShowSmoothLines = false
  Source = -> Connect
  Tolerance = 0.05
  ViewResult = <blob: 2837 chars omitted>
  Visible = true
  X = 140
  Y = 110
FEATURE [Drawing::FeatureViewPart] View006  label="HL"
  Direction = (-1,1,1)
  HiddenWidth = 0.15
  LineWidth = 0.35
  Rotation = 240
  Scale = 0.06
  ShowHiddenLines = false
  ShowSmoothLines = false
  Source = -> Connect
  Tolerance = 0.05
  ViewResult = <blob: 3664 chars omitted>
  Visible = true
  X = 170
  Y = 210
FEATURE [Drawing::FeatureViewPart] View007  label="VR001"
  Direction = (1,1,1)
  HiddenWidth = 0.15
  LineWidth = 0.35
  Rotation = 120
  Scale = 0.06
  ShowHiddenLines = false
  ShowSmoothLines = false
  Source = -> Connect
  Tolerance = 0.05
  ViewResult = <blob: 4146 chars omitted>
  Visible = true
  X = 70
  Y = 190
FEATURE [Drawing::FeaturePage] Page003  label="Gesamt2"
  EditableTexts = Manuel Dillmann | PC-Schrank | Gesamtansicht 3d | A4 | 4 / X | 0.08 | ... | ... | 17/04/2019 | REV A
  Group = -> [View004,View005,View006,View007]
  Template = C:/Program Files/FreeCAD 0.17/data/Mod/Drawing/Templates/A4_Portrait_ISO7200.svg
FEATURE [Part::Box] Box020  label="Würfel"
  AttacherType = Attacher::AttachEngine3D
  Height = 19
  Length = 2500
  Placement = pos=(10000,10000,10000) rot=(0,0,1;0rad)
  Width = 1250
FEATURE [Drawing::FeatureViewPart] Ortho010  label="PlatteRoh"
  Direction = (0,0,1)
  HiddenWidth = 0.15
  LineWidth = 0.85
  Rotation = 90
  Scale = 0.08
  ShowHiddenLines = false
  ShowSmoothLines = false
  Source = -> Box020
  Tolerance = 0.05
  ViewResult = <g id="PlatteRoh"\n   transform="rotate(90,-760,-787) translate(-760,-787) scale(0.08,0.08)"\n  >\n<g   fill="none"\n   stroke="rgb(0, 0, 0)"\n   stroke-linecap="butt"\n   stroke-linejoin="miter"\n   stroke-width="10.625000"\n   transform="scale(1,-1)"\n  >\n<path id= "1" d=" M 10000 10000 L 10000 11250 " />\n<path id= "2" d=" M 12500 10000 L 12500 11250 " />\n<path id= "3" d=" M 10000 10000 L 12500 10000 " />\n<path id= "4" d=" M 10000 11250 L 12500 11250 " />\n</g>\n</g>
  Visible = true
  X = -760
  Y = -787
FEATURE [Drawing::FeatureViewPart] Ortho011  label="Boden002"
  Direction = (0,0,1)
  HiddenWidth = 0.15
  LineWidth = 0.35
  Rotation = 90
  Scale = 0.08
  ShowHiddenLines = false
  ShowSmoothLines = false
  Source = -> Box
  Tolerance = 0.05
  ViewResult = <g id="Boden002"\n   transform="rotate(90,41,14) translate(41,14) scale(0.08,0.08)"\n  >\n<g   fill="none"\n   stroke="rgb(0, 0, 0)"\n   stroke-linecap="butt"\n   stroke-linejoin="miter"\n   stroke-width="4.375000"\n   transform="scale(1,-1)"\n  >\n<path id= "1" d=" M 0 0 L 0 300 " />\n<path id= "2" d=" M 750 0 L 750 300 " />\n<path id= "3" d=" M 0 0 L 750 0 " />\n<path id= "4" d=" M 0 300 L 750 300 " />\n</g>\n</g>
  Visible = true
  X = 41
  Y = 14
FEATURE [Drawing::FeatureViewPython] text011  label="BodenStr"  # drawing view (typed FeaturePython)
  Rotation = 0
  ViewResult = <g> <text x="60.000000" y="65.000000" font-family="inherit" font-size="5" fill="rgb(0,0,0)" text-anchor="inherit" transform="rotate(270.000000 60.000000,65.000000)" >Boden</text> </g>
  Visible = true
  X = 0
  Y = 0
  click1_x = 60
  click1_y = 65
  rotation = 270
  text = Boden
  textRenderer_addText_color = rgb(0,0,0)
  textRenderer_addText_family = inherit
  textRenderer_addText_size = 5
FEATURE [Drawing::FeatureViewPart] Ortho012  label="Mittelebene002"
  Direction = (0,0,1)
  HiddenWidth = 0.15
  LineWidth = 0.35
  Rotation = 90
  Scale = 0.08
  ShowHiddenLines = false
  ShowSmoothLines = false
  Source = -> Box001
  Tolerance = 0.05
  ViewResult = <g id="Mittelebene002"\n   transform="rotate(90,65.5,14) translate(65.5,14) scale(0.08,0.08)"\n  >\n<g   fill="none"\n   stroke="rgb(0, 0, 0)"\n   stroke-linecap="butt"\n   stroke-linejoin="miter"\n   stroke-width="4.375000"\n   transform="scale(1,-1)"\n  >\n<path id= "1" d=" M 0 0 L 0 300 " />\n<path id= "2" d=" M 731 0 L 731 300 " />\n<path id= "3" d=" M 0 0 L 731 0 " />\n<path id= "4" d=" M 0 300 L 731 300 " />\n</g>\n</g>
  Visible = true
  X = 65.5
  Y = 14
FEATURE [Drawing::FeatureViewPython] text012  label="MittelebeneStr"  # drawing view (typed FeaturePython)
  Rotation = 0
  ViewResult = <g> <text x="83.000000" y="65.000000" font-family="inherit" font-size="5" fill="rgb(0,0,0)" text-anchor="inherit" transform="rotate(270.000000 83.000000,65.000000)" >Mittelebene</text> </g>
  Visible = true
  X = 0
  Y = 0
  click1_x = 83
  click1_y = 65
  rotation = 270
  text = Mittelebene
  textRenderer_addText_color = rgb(0,0,0)
  textRenderer_addText_family = inherit
  textRenderer_addText_size = 5
FEATURE [Drawing::FeatureViewPart] Ortho013  label="Deckel002"
  Direction = (0,0,1)
  HiddenWidth = 0.15
  LineWidth = 0.35
  Rotation = 90
  Scale = 0.08
  ShowHiddenLines = false
  ShowSmoothLines = false
  Source = -> Box002
  Tolerance = 0.05
  ViewResult = <g id="Deckel002"\n   transform="rotate(90,90,14) translate(90,14) scale(0.08,0.08)"\n  >\n<g   fill="none"\n   stroke="rgb(0, 0, 0)"\n   stroke-linecap="butt"\n   stroke-linejoin="miter"\n   stroke-width="4.375000"\n   transform="scale(1,-1)"\n  >\n<path id= "1" d=" M 0 0 L 0 300 " />\n<path id= "2" d=" M 731 0 L 731 300 " />\n<path id= "3" d=" M 0 0 L 731 0 " />\n<path id= "4" d=" M 0 300 L 731 300 " />\n</g>\n</g>
  Visible = true
  X = 90
  Y = 14
FEATURE [Drawing::FeatureViewPython] text013  label="DeckelStr"  # drawing view (typed FeaturePython)
  Rotation = 0
  ViewResult = <g> <text x="105.000000" y="65.000000" font-family="inherit" font-size="5" fill="rgb(0,0,0)" text-anchor="inherit" transform="rotate(270.000000 105.000000,65.000000)" >Deckel</text> </g>
  Visible = true
  X = 0
  Y = 0
  click1_x = 105
  click1_y = 65
  rotation = 270
  text = Deckel
  textRenderer_addText_color = rgb(0,0,0)
  textRenderer_addText_family = inherit
  textRenderer_addText_size = 5
FEATURE [Drawing::FeatureViewPart] Ortho014  label="SeiteLi002"
  Direction = (1,0,0)
  HiddenWidth = 0.15
  LineWidth = 0.35
  Rotation = -90
  Scale = 0.08
  ShowHiddenLines = false
  ShowSmoothLines = false
  Source = -> Box003
  Tolerance = 0.05
  ViewResult = <g id="Ortho_0_010"\n   transform="rotate(-90,115,118) translate(115,118) scale(0.08,0.08)"\n  >\n<g   fill="none"\n   stroke="rgb(0, 0, 0)"\n   stroke-linecap="butt"\n   stroke-linejoin="miter"\n   stroke-width="4.375000"\n   transform="scale(1,-1)"\n  >\n<path id= "1" d=" M 0 0 L 1300 0 " />\n<path id= "2" d=" M 1300 0 L 1300 -300 " />\n<path id= "3" d=" M 0 -300 L 1300 -300 " />\n<path id= "4" d=" M 0 0 L 0 -300 " />\n</g>\n</g>
  Visible = true
  X = 115
  Y = 118
FEATURE [Drawing::FeatureViewPython] text014  label="SeiteLiStr"  # drawing view (typed FeaturePython)
  Rotation = 0
  ViewResult = <g> <text x="130.000000" y="85.000000" font-family="inherit" font-size="5" fill="rgb(0,0,0)" text-anchor="inherit" transform="rotate(270.000000 130.000000,85.000000)" >Seite Links</text> </g>
  Visible = true
  X = 0
  Y = 0
  click1_x = 130
  click1_y = 85
  rotation = 270
  text = Seite Links
  textRenderer_addText_color = rgb(0,0,0)
  textRenderer_addText_family = inherit
  textRenderer_addText_size = 5
FEATURE [Drawing::FeatureViewPart] Ortho015  label="SeiteRe002"
  Direction = (1,0,0)
  HiddenWidth = 0.15
  LineWidth = 0.35
  Rotation = -90
  Scale = 0.08
  ShowHiddenLines = false
  ShowSmoothLines = false
  Source = -> Box004
  Tolerance = 0.05
  ViewResult = <g id="Ortho_0_010"\n   transform="rotate(-90,115,223) translate(115,223) scale(0.08,0.08)"\n  >\n<g   fill="none"\n   stroke="rgb(0, 0, 0)"\n   stroke-linecap="butt"\n   stroke-linejoin="miter"\n   stroke-width="4.375000"\n   transform="scale(1,-1)"\n  >\n<path id= "1" d=" M 700 0 L 1300 0 " />\n<path id= "2" d=" M 1300 0 L 1300 -300 " />\n<path id= "3" d=" M 700 -300 L 1300 -300 " />\n<path id= "4" d=" M 700 0 L 700 -300 " />\n</g>\n</g>
  Visible = true
  X = 115
  Y = 223
FEATURE [Drawing::FeatureViewPython] text015  label="SeiteReStr"  # drawing view (typed FeaturePython)
  Rotation = 0
  ViewResult = <g> <text x="131.181547" y="157.872164" font-family="inherit" font-size="5" fill="rgb(0,0,0)" text-anchor="inherit" transform="rotate(270.000000 131.181547,157.872164)" >Seite Rechts</text> </g>
  Visible = true
  X = 0
  Y = 0
  click1_x = 131.182
  click1_y = 157.872
  rotation = 270
  text = Seite Rechts
  textRenderer_addText_color = rgb(0,0,0)
  textRenderer_addText_family = inherit
  textRenderer_addText_size = 5
FEATURE [Drawing::FeatureViewPart] Ortho016  label="AbdeckungVo002"
  Direction = (0,1,0)
  HiddenWidth = 0.15
  LineWidth = 0.35
  Rotation = 270
  Scale = 0.08
  ShowHiddenLines = false
  ShowSmoothLines = false
  Source = -> Box005
  Tolerance = 0.05
  ViewResult = <g id="AbdeckungVo002"\n   transform="rotate(270,101,163) translate(101,163) scale(0.08,0.08)"\n  >\n<g   fill="none"\n   stroke="rgb(0, 0, 0)"\n   stroke-linecap="butt"\n   stroke-linejoin="miter"\n   stroke-width="4.375000"\n   transform="scale(1,-1)"\n  >\n<path id= "1" d=" M 0 200 L 705 200 " />\n<path id= "2" d=" M 0 750 L 705 750 " />\n<path id= "3" d=" M 0 200 L 0 750 " />\n<path id= "4" d=" M 705 200 L 705 750 " />\n</g>\n</g>
  Visible = true
  X = 101
  Y = 163
FEATURE [Drawing::FeatureViewPython] text016  label="AbdeckungVoStr"  # drawing view (typed FeaturePython)
  Rotation = 0
  ViewResult = <g> <text x="46.000000" y="150.000000" font-family="inherit" font-size="5" fill="rgb(0,0,0)" text-anchor="inherit" transform="rotate(0.000000 46.000000,150.000000)" >Abdeckung Vorne</text> </g>
  Visible = true
  X = 0
  Y = 0
  click1_x = 46
  click1_y = 150
  rotation = 0
  text = Abdeckung Vorne
  textRenderer_addText_color = rgb(0,0,0)
  textRenderer_addText_family = inherit
  textRenderer_addText_size = 5
FEATURE [Drawing::FeatureViewPart] Ortho017  label="Tuere002"
  Direction = (0,1,0)
  HiddenWidth = 0.15
  LineWidth = 0.35
  Rotation = 270
  Scale = 0.08
  ShowHiddenLines = false
  ShowSmoothLines = false
  Source = -> Box006
  Tolerance = 0.05
  ViewResult = <g id="Tuere002"\n   transform="rotate(270,102,163) translate(102,163) scale(0.08,0.08)"\n  >\n<g   fill="none"\n   stroke="rgb(0, 0, 0)"\n   stroke-linecap="butt"\n   stroke-linejoin="miter"\n   stroke-width="4.375000"\n   transform="scale(1,-1)"\n  >\n<path id= "1" d=" M 0 -19 L 705 -19 " />\n<path id= "2" d=" M 0 200 L 705 200 " />\n<path id= "3" d=" M 0 -19 L 0 200 " />\n<path id= "4" d=" M 705 -19 L 705 200 " />\n</g>\n</g>
  Visible = true
  X = 102
  Y = 163
FEATURE [Drawing::FeatureViewPython] text017  label="TuereStr"  # drawing view (typed FeaturePython)
  Rotation = 0
  ViewResult = <g> <text x="95.000000" y="150.000000" font-family="inherit" font-size="5" fill="rgb(0,0,0)" text-anchor="inherit" transform="rotate(270.000000 95.000000,150.000000)" >Türe</text> </g>
  Visible = true
  X = 0
  Y = 0
  click1_x = 95
  click1_y = 150
  rotation = 270
  text = Türe
  textRenderer_addText_color = rgb(0,0,0)
  textRenderer_addText_family = inherit
  textRenderer_addText_size = 5
FEATURE [Drawing::FeatureViewPart] Ortho018  label="StuetzeMi002"
  Direction = (1,0,0)
  HiddenWidth = 0.15
  LineWidth = 0.35
  Rotation = 0
  Scale = 0.08
  ShowHiddenLines = false
  ShowSmoothLines = false
  Source = -> Box007
  Tolerance = 0.05
  ViewResult = <g id="StuetzeMi002"\n   transform="rotate(0,40,80) translate(40,80) scale(0.08,0.08)"\n  >\n<g   fill="none"\n   stroke="rgb(0, 0, 0)"\n   stroke-linecap="butt"\n   stroke-linejoin="miter"\n   stroke-width="4.375000"\n   transform="scale(1,-1)"\n  >\n<path id= "1" d=" M 19 0 L 700 0 " />\n<path id= "2" d=" M 700 0 L 700 -300 " />\n<path id= "3" d=" M 19 -300 L 700 -300 " />\n<path id= "4" d=" M 19 0 L 19 -300 " />\n</g>\n</g>
  Visible = true
  X = 40
  Y = 80
FEATURE [Drawing::FeatureViewPython] text018  label="StuetzeMiStr"  # drawing view (typed FeaturePython)
  Rotation = 0
  ViewResult = <g> <text x="48.000000" y="100.000000" font-family="inherit" font-size="5" fill="rgb(0,0,0)" text-anchor="inherit" transform="rotate(0.000000 48.000000,100.000000)" >Stütze Mitte</text> </g>
  Visible = true
  X = 0
  Y = 0
  click1_x = 48
  click1_y = 100
  rotation = 0
  text = Stütze Mitte
  textRenderer_addText_color = rgb(0,0,0)
  textRenderer_addText_family = inherit
  textRenderer_addText_size = 5
FEATURE [Drawing::FeatureViewPython] dim022  label="Platte1"  # drawing view (typed FeaturePython)
  Rotation = 0
  ViewResult = <g> \n  <line x1="40.000000" y1="215.000000" x2="40.000000" y2="223.043224" style="stroke:rgb(0,0,255);stroke-width:0.50" />\n<line x1="140.000000" y1="215.000000" x2="140.000000" y2="223.043224" style="stroke:rgb(0,0,255);stroke-width:0.50" />\n<line x1="40.000000" y1="222.043224" x2="140.000000" y2="222.043224" style="stroke:rgb(0,0,255);stroke-width:0.50" /> \n  <polygon points="140.000000,222.043224 137.000000,221.043224 136.000000,222.043224 137.000000,223.043224" style="fill:rgb(0,0,255);stroke:rgb(0,0,255);stroke-width:0" /><polygon points="40.000000,222.043224 43.000000,223.043224 44.000000,222.043224 43.000000,221.043224" style="fill:rgb(0,0,255);stroke:rgb(0,0,255);stroke-width:0" /> \n  <text x="90.000000" y="220.043224" font-family="inherit" font-size="3.6" fill="rgb(0,0,255)" text-anchor="middle" transform="rotate(0.000000 90.000000,220.043224)" >1250</text> </g>
  Visible = true
  X = 0
  Y = 0
  arrowL1 = 3
  arrowL2 = 1
  arrowW = 2
  arrow_scheme = 0
  autoPlaceOffset = 2
  autoPlaceText = true
  click1_x = 76.0967
  click1_y = 222.043
  click2_x = 76.0967
  click2_y = 222.043
  comma_decimal_place = false
  dimension_line_overshoot = 1
  gap_datum_points = 2
  halfDimension_linear = false
  lineColor = rgb(0,0,255)
  strokeWidth = 0.5
  textFormat_linear = %(value)3.3f
  textRenderer_color = rgb(0,0,255)
  textRenderer_family = inherit
  textRenderer_size = 3.6
  unit_custom_scale = 1
  unit_scheme = 0
FEATURE [Drawing::FeatureViewPython] dim023  label="Platte2"  # drawing view (typed FeaturePython)
  Rotation = 0
  ViewResult = <g> \n  <line x1="142.000000" y1="13.000000" x2="156.032737" y2="13.000000" style="stroke:rgb(0,0,255);stroke-width:0.50" />\n<line x1="142.000000" y1="213.000000" x2="156.032737" y2="213.000000" style="stroke:rgb(0,0,255);stroke-width:0.50" />\n<line x1="155.032737" y1="13.000000" x2="155.032737" y2="213.000000" style="stroke:rgb(0,0,255);stroke-width:0.50" /> \n  <polygon points="155.032737,213.000000 156.032737,210.000000 155.032737,209.000000 154.032737,210.000000" style="fill:rgb(0,0,255);stroke:rgb(0,0,255);stroke-width:0" /><polygon points="155.032737,13.000000 154.032737,16.000000 155.032737,17.000000 156.032737,16.000000" style="fill:rgb(0,0,255);stroke:rgb(0,0,255);stroke-width:0" /> \n  <text x="153.032737" y="113.000000" font-family="inherit" font-size="3.6" fill="rgb(0,0,255)" text-anchor="middle" transform="rotate(-90.000000 153.032737,113.000000)" >2500</text> </g>
  Visible = true
  X = 0
  Y = 0
  arrowL1 = 3
  arrowL2 = 1
  arrowW = 2
  arrow_scheme = 0
  autoPlaceOffset = 2
  autoPlaceText = true
  click1_x = 155.033
  click1_y = 178.884
  click2_x = 155.033
  click2_y = 178.884
  comma_decimal_place = false
  dimension_line_overshoot = 1
  gap_datum_points = 2
  halfDimension_linear = false
  lineColor = rgb(0,0,255)
  strokeWidth = 0.5
  textFormat_linear = %(value)3.3f
  textRenderer_color = rgb(0,0,255)
  textRenderer_family = inherit
  textRenderer_size = 3.6
  unit_custom_scale = 1
  unit_scheme = 0
FEATURE [Drawing::FeatureViewPython] dim038  # drawing view (typed FeaturePython)
  Rotation = 0
  ViewResult = <g> \n  <line x1="115.000000" y1="16.000000" x2="115.000000" y2="24.188657" style="stroke:rgb(0,0,255);stroke-width:0.50" />\n<line x1="139.000000" y1="16.000000" x2="139.000000" y2="24.188657" style="stroke:rgb(0,0,255);stroke-width:0.50" />\n<line x1="115.000000" y1="23.188657" x2="139.000000" y2="23.188657" style="stroke:rgb(0,0,255);stroke-width:0.50" /> \n  <polygon points="139.000000,23.188657 136.000000,22.188657 135.000000,23.188657 136.000000,24.188657" style="fill:rgb(0,0,255);stroke:rgb(0,0,255);stroke-width:0" /><polygon points="115.000000,23.188657 118.000000,24.188657 119.000000,23.188657 118.000000,22.188657" style="fill:rgb(0,0,255);stroke:rgb(0,0,255);stroke-width:0" /> \n  <text x="127.000000" y="21.188657" font-family="inherit" font-size="3.6" fill="rgb(0,0,255)" text-anchor="middle" transform="rotate(0.000000 127.000000,21.188657)" >300</text> </g>
  Visible = true
  X = 0
  Y = 0
  arrowL1 = 3
  arrowL2 = 1
  arrowW = 2
  arrow_scheme = 0
  autoPlaceOffset = 2
  autoPlaceText = true
  click1_x = 122.095
  click1_y = 23.1887
  click2_x = 122.095
  click2_y = 23.1887
  comma_decimal_place = false
  dimension_line_overshoot = 1
  gap_datum_points = 2
  halfDimension_linear = false
  lineColor = rgb(0,0,255)
  strokeWidth = 0.5
  textFormat_linear = %(value)3.3f
  textRenderer_color = rgb(0,0,255)
  textRenderer_family = inherit
  textRenderer_size = 3.6
  unit_custom_scale = 1
  unit_scheme = 0
FEATURE [Drawing::FeatureViewPython] dim039  # drawing view (typed FeaturePython)
  Rotation = 0
  ViewResult = <g> \n  <line x1="117.000000" y1="118.000000" x2="122.622141" y2="118.000000" style="stroke:rgb(0,0,255);stroke-width:0.50" />\n<line x1="117.000000" y1="14.000000" x2="122.622141" y2="14.000000" style="stroke:rgb(0,0,255);stroke-width:0.50" />\n<line x1="121.622141" y1="118.000000" x2="121.622141" y2="14.000000" style="stroke:rgb(0,0,255);stroke-width:0.50" /> \n  <polygon points="121.622141,14.000000 120.622141,17.000000 121.622141,18.000000 122.622141,17.000000" style="fill:rgb(0,0,255);stroke:rgb(0,0,255);stroke-width:0" /><polygon points="121.622141,118.000000 122.622141,115.000000 121.622141,114.000000 120.622141,115.000000" style="fill:rgb(0,0,255);stroke:rgb(0,0,255);stroke-width:0" /> \n  <text x="119.622141" y="66.000000" font-family="inherit" font-size="3.6" fill="rgb(0,0,255)" text-anchor="middle" transform="rotate(-90.000000 119.622141,66.000000)" >1300</text> </g>
  Visible = true
  X = 0
  Y = 0
  arrowL1 = 3
  arrowL2 = 1
  arrowW = 2
  arrow_scheme = 0
  autoPlaceOffset = 2
  autoPlaceText = true
  click1_x = 121.622
  click1_y = 41.1717
  click2_x = 121.622
  click2_y = 41.1717
  comma_decimal_place = false
  dimension_line_overshoot = 1
  gap_datum_points = 2
  halfDimension_linear = false
  lineColor = rgb(0,0,255)
  strokeWidth = 0.5
  textFormat_linear = %(value)3.3f
  textRenderer_color = rgb(0,0,255)
  textRenderer_family = inherit
  textRenderer_size = 3.6
  unit_custom_scale = 1
  unit_scheme = 0
FEATURE [Drawing::FeatureViewPython] dim040  # drawing view (typed FeaturePython)
  Rotation = 0
  ViewResult = <g> \n  <line x1="115.000000" y1="121.000000" x2="115.000000" y2="125.934806" style="stroke:rgb(0,0,255);stroke-width:0.50" />\n<line x1="139.000000" y1="121.000000" x2="139.000000" y2="125.934806" style="stroke:rgb(0,0,255);stroke-width:0.50" />\n<line x1="115.000000" y1="124.934806" x2="139.000000" y2="124.934806" style="stroke:rgb(0,0,255);stroke-width:0.50" /> \n  <polygon points="139.000000,124.934806 136.000000,123.934806 135.000000,124.934806 136.000000,125.934806" style="fill:rgb(0,0,255);stroke:rgb(0,0,255);stroke-width:0" /><polygon points="115.000000,124.934806 118.000000,125.934806 119.000000,124.934806 118.000000,123.934806" style="fill:rgb(0,0,255);stroke:rgb(0,0,255);stroke-width:0" /> \n  <text x="127.000000" y="122.934806" font-family="inherit" font-size="3.6" fill="rgb(0,0,255)" text-anchor="middle" transform="rotate(0.000000 127.000000,122.934806)" >300</text> </g>
  Visible = true
  X = 0
  Y = 0
  arrowL1 = 3
  arrowL2 = 1
  arrowW = 2
  arrow_scheme = 0
  autoPlaceOffset = 2
  autoPlaceText = true
  click1_x = 128.247
  click1_y = 124.935
  click2_x = 128.247
  click2_y = 124.935
  comma_decimal_place = false
  dimension_line_overshoot = 1
  gap_datum_points = 2
  halfDimension_linear = false
  lineColor = rgb(0,0,255)
  strokeWidth = 0.5
  textFormat_linear = %(value)3.3f
  textRenderer_color = rgb(0,0,255)
  textRenderer_family = inherit
  textRenderer_size = 3.6
  unit_custom_scale = 1
  unit_scheme = 0
FEATURE [Drawing::FeatureViewPython] dim041  # drawing view (typed FeaturePython)
  Rotation = 0
  ViewResult = <g> \n  <line x1="117.000000" y1="167.000000" x2="122.622141" y2="167.000000" style="stroke:rgb(0,0,255);stroke-width:0.50" />\n<line x1="117.000000" y1="119.000000" x2="122.622141" y2="119.000000" style="stroke:rgb(0,0,255);stroke-width:0.50" />\n<line x1="121.622141" y1="167.000000" x2="121.622141" y2="119.000000" style="stroke:rgb(0,0,255);stroke-width:0.50" /> \n  <polygon points="121.622141,119.000000 120.622141,122.000000 121.622141,123.000000 122.622141,122.000000" style="fill:rgb(0,0,255);stroke:rgb(0,0,255);stroke-width:0" /><polygon points="121.622141,167.000000 122.622141,164.000000 121.622141,163.000000 120.622141,164.000000" style="fill:rgb(0,0,255);stroke:rgb(0,0,255);stroke-width:0" /> \n  <text x="119.622141" y="143.000000" font-family="inherit" font-size="3.6" fill="rgb(0,0,255)" text-anchor="middle" transform="rotate(-90.000000 119.622141,143.000000)" >600</text> </g>
  Visible = true
  X = 0
  Y = 0
  arrowL1 = 3
  arrowL2 = 1
  arrowW = 2
  arrow_scheme = 0
  autoPlaceOffset = 2
  autoPlaceText = true
  click1_x = 121.622
  click1_y = 140.552
  click2_x = 121.622
  click2_y = 140.552
  comma_decimal_place = false
  dimension_line_overshoot = 1
  gap_datum_points = 2
  halfDimension_linear = false
  lineColor = rgb(0,0,255)
  strokeWidth = 0.5
  textFormat_linear = %(value)3.3f
  textRenderer_color = rgb(0,0,255)
  textRenderer_family = inherit
  textRenderer_size = 3.6
  unit_custom_scale = 1
  unit_scheme = 0
FEATURE [Drawing::FeatureViewPart] Ortho019  label="Klappe002"
  Direction = (0,1,0)
  HiddenWidth = 0.15
  LineWidth = 0.35
  Rotation = 90
  Scale = 0.08
  ShowHiddenLines = false
  ShowSmoothLines = false
  Source = -> Box008
  Tolerance = 0.05
  ViewResult = <g id="Klappe002"\n   transform="rotate(90,43,108) translate(43,108) scale(0.08,0.08)"\n  >\n<g   fill="none"\n   stroke="rgb(0, 0, 0)"\n   stroke-linecap="butt"\n   stroke-linejoin="miter"\n   stroke-width="4.375000"\n   transform="scale(1,-1)"\n  >\n<path id= "1" d=" M 705 -19 L 1300 -19 " />\n<path id= "2" d=" M 705 750 L 1300 750 " />\n<path id= "3" d=" M 705 -19 L 705 750 " />\n<path id= "4" d=" M 1300 -19 L 1300 750 " />\n</g>\n</g>
  Visible = true
  X = 43
  Y = 108
FEATURE [Drawing::FeatureViewPython] text019  label="KlappeStr"  # drawing view (typed FeaturePython)
  Rotation = 0
  ViewResult = <g> <text x="50.541808" y="195.920492" font-family="inherit" font-size="5" fill="rgb(0,0,0)" text-anchor="inherit" transform="rotate(0.000000 50.541808,195.920492)" >Klappe</text> </g>
  Visible = true
  X = 0
  Y = 0
  click1_x = 50.5418
  click1_y = 195.92
  rotation = 0
  text = Klappe
  textRenderer_addText_color = rgb(0,0,0)
  textRenderer_addText_family = inherit
  textRenderer_addText_size = 5
FEATURE [Drawing::FeatureViewPart] Ortho020  label="StuetzeHi002"
  Direction = (0,1,0)
  HiddenWidth = 0.15
  LineWidth = 0.35
  Rotation = 90
  Scale = 0.08
  ShowHiddenLines = false
  ShowSmoothLines = false
  Source = -> Box009
  Tolerance = 0.05
  ViewResult = <g id="StuetzeHi002"\n   transform="rotate(90,53,107) translate(53,107) scale(0.08,0.08)"\n  >\n<g   fill="none"\n   stroke="rgb(0, 0, 0)"\n   stroke-linecap="butt"\n   stroke-linejoin="miter"\n   stroke-width="4.375000"\n   transform="scale(1,-1)"\n  >\n<path id= "1" d=" M 19 650 L 700 650 " />\n<path id= "2" d=" M 19 750 L 700 750 " />\n<path id= "3" d=" M 19 650 L 19 750 " />\n<path id= "4" d=" M 700 650 L 700 750 " />\n</g>\n</g>
  Visible = true
  X = 53
  Y = 107
FEATURE [Drawing::FeatureViewPython] text020  label="StuetzeHiStr"  # drawing view (typed FeaturePython)
  Rotation = 0
  ViewResult = <g> <text x="111.500000" y="158.440050" font-family="inherit" font-size="5" fill="rgb(0,0,0)" text-anchor="inherit" transform="rotate(270.000000 111.500000,158.440050)" >Stütze Hi</text> </g>
  Visible = true
  X = 0
  Y = 0
  click1_x = 111.5
  click1_y = 158.44
  rotation = 270
  text = Stütze Hi
  textRenderer_addText_color = rgb(0,0,0)
  textRenderer_addText_family = inherit
  textRenderer_addText_size = 5
FEATURE [Drawing::FeatureViewPython] dim024  # drawing view (typed FeaturePython)
  Rotation = 0
  ViewResult = <g> \n  <line x1="43.000000" y1="14.000000" x2="49.270266" y2="14.000000" style="stroke:rgb(0,0,255);stroke-width:0.50" />\n<line x1="43.000000" y1="74.000000" x2="49.270266" y2="74.000000" style="stroke:rgb(0,0,255);stroke-width:0.50" />\n<line x1="48.270266" y1="14.000000" x2="48.270266" y2="74.000000" style="stroke:rgb(0,0,255);stroke-width:0.50" /> \n  <polygon points="48.270266,74.000000 49.270266,71.000000 48.270266,70.000000 47.270266,71.000000" style="fill:rgb(0,0,255);stroke:rgb(0,0,255);stroke-width:0" /><polygon points="48.270266,14.000000 47.270266,17.000000 48.270266,18.000000 49.270266,17.000000" style="fill:rgb(0,0,255);stroke:rgb(0,0,255);stroke-width:0" /> \n  <text x="46.270266" y="44.000000" font-family="inherit" font-size="3.6" fill="rgb(0,0,255)" text-anchor="middle" transform="rotate(-90.000000 46.270266,44.000000)" >750</text> </g>
  Visible = true
  X = 0
  Y = 0
  arrowL1 = 3
  arrowL2 = 1
  arrowW = 2
  arrow_scheme = 0
  autoPlaceOffset = 2
  autoPlaceText = true
  click1_x = 48.2703
  click1_y = 39.1841
  click2_x = 48.2703
  click2_y = 39.1841
  comma_decimal_place = false
  dimension_line_overshoot = 1
  gap_datum_points = 2
  halfDimension_linear = false
  lineColor = rgb(0,0,255)
  strokeWidth = 0.5
  textFormat_linear = %(value)3.3f
  textRenderer_color = rgb(0,0,255)
  textRenderer_family = inherit
  textRenderer_size = 3.6
  unit_custom_scale = 1
  unit_scheme = 0
FEATURE [Drawing::FeatureViewPython] dim025  # drawing view (typed FeaturePython)
  Rotation = 0
  ViewResult = <g> \n  <line x1="41.000000" y1="16.000000" x2="41.000000" y2="22.579648" style="stroke:rgb(0,0,255);stroke-width:0.50" />\n<line x1="65.000000" y1="16.000000" x2="65.000000" y2="22.579648" style="stroke:rgb(0,0,255);stroke-width:0.50" />\n<line x1="41.000000" y1="21.579648" x2="65.000000" y2="21.579648" style="stroke:rgb(0,0,255);stroke-width:0.50" /> \n  <polygon points="65.000000,21.579648 62.000000,20.579648 61.000000,21.579648 62.000000,22.579648" style="fill:rgb(0,0,255);stroke:rgb(0,0,255);stroke-width:0" /><polygon points="41.000000,21.579648 44.000000,22.579648 45.000000,21.579648 44.000000,20.579648" style="fill:rgb(0,0,255);stroke:rgb(0,0,255);stroke-width:0" /> \n  <text x="53.000000" y="19.579648" font-family="inherit" font-size="3.6" fill="rgb(0,0,255)" text-anchor="middle" transform="rotate(0.000000 53.000000,19.579648)" >300</text> </g>
  Visible = true
  X = 0
  Y = 0
  arrowL1 = 3
  arrowL2 = 1
  arrowW = 2
  arrow_scheme = 0
  autoPlaceOffset = 2
  autoPlaceText = true
  click1_x = 53.9491
  click1_y = 21.5796
  click2_x = 53.9491
  click2_y = 21.5796
  comma_decimal_place = false
  dimension_line_overshoot = 1
  gap_datum_points = 2
  halfDimension_linear = false
  lineColor = rgb(0,0,255)
  strokeWidth = 0.5
  textFormat_linear = %(value)3.3f
  textRenderer_color = rgb(0,0,255)
  textRenderer_family = inherit
  textRenderer_size = 3.6
  unit_custom_scale = 1
  unit_scheme = 0
FEATURE [Drawing::FeatureViewPython] dim026  # drawing view (typed FeaturePython)
  Rotation = 0
  ViewResult = <g> \n  <line x1="65.500000" y1="16.000000" x2="65.500000" y2="22.579648" style="stroke:rgb(0,0,255);stroke-width:0.50" />\n<line x1="89.500000" y1="16.000000" x2="89.500000" y2="22.579648" style="stroke:rgb(0,0,255);stroke-width:0.50" />\n<line x1="65.500000" y1="21.579648" x2="89.500000" y2="21.579648" style="stroke:rgb(0,0,255);stroke-width:0.50" /> \n  <polygon points="89.500000,21.579648 86.500000,20.579648 85.500000,21.579648 86.500000,22.579648" style="fill:rgb(0,0,255);stroke:rgb(0,0,255);stroke-width:0" /><polygon points="65.500000,21.579648 68.500000,22.579648 69.500000,21.579648 68.500000,20.579648" style="fill:rgb(0,0,255);stroke:rgb(0,0,255);stroke-width:0" /> \n  <text x="77.500000" y="19.579648" font-family="inherit" font-size="3.6" fill="rgb(0,0,255)" text-anchor="middle" transform="rotate(0.000000 77.500000,19.579648)" >300</text> </g>
  Visible = true
  X = 0
  Y = 0
  arrowL1 = 3
  arrowL2 = 1
  arrowW = 2
  arrow_scheme = 0
  autoPlaceOffset = 2
  autoPlaceText = true
  click1_x = 78.3682
  click1_y = 21.5796
  click2_x = 78.3682
  click2_y = 21.5796
  comma_decimal_place = false
  dimension_line_overshoot = 1
  gap_datum_points = 2
  halfDimension_linear = false
  lineColor = rgb(0,0,255)
  strokeWidth = 0.5
  textFormat_linear = %(value)3.3f
  textRenderer_color = rgb(0,0,255)
  textRenderer_family = inherit
  textRenderer_size = 3.6
  unit_custom_scale = 1
  unit_scheme = 0
FEATURE [Drawing::FeatureViewPython] dim027  # drawing view (typed FeaturePython)
  Rotation = 0
  ViewResult = <g> \n  <line x1="67.500000" y1="14.000000" x2="74.257227" y2="14.000000" style="stroke:rgb(0,0,255);stroke-width:0.50" />\n<line x1="67.500000" y1="72.480000" x2="74.257227" y2="72.480000" style="stroke:rgb(0,0,255);stroke-width:0.50" />\n<line x1="73.257227" y1="14.000000" x2="73.257227" y2="72.480000" style="stroke:rgb(0,0,255);stroke-width:0.50" /> \n  <polygon points="73.257227,72.480000 74.257227,69.480000 73.257227,68.480000 72.257227,69.480000" style="fill:rgb(0,0,255);stroke:rgb(0,0,255);stroke-width:0" /><polygon points="73.257227,14.000000 72.257227,17.000000 73.257227,18.000000 74.257227,17.000000" style="fill:rgb(0,0,255);stroke:rgb(0,0,255);stroke-width:0" /> \n  <text x="71.257227" y="43.240000" font-family="inherit" font-size="3.6" fill="rgb(0,0,255)" text-anchor="middle" transform="rotate(-90.000000 71.257227,43.240000)" >731</text> </g>
  Visible = true
  X = 0
  Y = 0
  arrowL1 = 3
  arrowL2 = 1
  arrowW = 2
  arrow_scheme = 0
  autoPlaceOffset = 2
  autoPlaceText = true
  click1_x = 73.2572
  click1_y = 35.7768
  click2_x = 73.2572
  click2_y = 35.7768
  comma_decimal_place = false
  dimension_line_overshoot = 1
  gap_datum_points = 2
  halfDimension_linear = false
  lineColor = rgb(0,0,255)
  strokeWidth = 0.5
  textFormat_linear = %(value)3.3f
  textRenderer_color = rgb(0,0,255)
  textRenderer_family = inherit
  textRenderer_size = 3.6
  unit_custom_scale = 1
  unit_scheme = 0
FEATURE [Drawing::FeatureViewPython] dim028  # drawing view (typed FeaturePython)
  Rotation = 0
  ViewResult = <g> \n  <line x1="90.000000" y1="16.000000" x2="90.000000" y2="22.011763" style="stroke:rgb(0,0,255);stroke-width:0.50" />\n<line x1="114.000000" y1="16.000000" x2="114.000000" y2="22.011763" style="stroke:rgb(0,0,255);stroke-width:0.50" />\n<line x1="90.000000" y1="21.011763" x2="114.000000" y2="21.011763" style="stroke:rgb(0,0,255);stroke-width:0.50" /> \n  <polygon points="114.000000,21.011763 111.000000,20.011763 110.000000,21.011763 111.000000,22.011763" style="fill:rgb(0,0,255);stroke:rgb(0,0,255);stroke-width:0" /><polygon points="90.000000,21.011763 93.000000,22.011763 94.000000,21.011763 93.000000,20.011763" style="fill:rgb(0,0,255);stroke:rgb(0,0,255);stroke-width:0" /> \n  <text x="102.000000" y="19.011763" font-family="inherit" font-size="3.6" fill="rgb(0,0,255)" text-anchor="middle" transform="rotate(0.000000 102.000000,19.011763)" >300</text> </g>
  Visible = true
  X = 0
  Y = 0
  arrowL1 = 3
  arrowL2 = 1
  arrowW = 2
  arrow_scheme = 0
  autoPlaceOffset = 2
  autoPlaceText = true
  click1_x = 99.9478
  click1_y = 21.0118
  click2_x = 99.9478
  click2_y = 21.0118
  comma_decimal_place = false
  dimension_line_overshoot = 1
  gap_datum_points = 2
  halfDimension_linear = false
  lineColor = rgb(0,0,255)
  strokeWidth = 0.5
  textFormat_linear = %(value)3.3f
  textRenderer_color = rgb(0,0,255)
  textRenderer_family = inherit
  textRenderer_size = 3.6
  unit_custom_scale = 1
  unit_scheme = 0
FEATURE [Drawing::FeatureViewPython] dim029  # drawing view (typed FeaturePython)
  Rotation = 0
  ViewResult = <g> \n  <line x1="92.000000" y1="14.000000" x2="98.108418" y2="14.000000" style="stroke:rgb(0,0,255);stroke-width:0.50" />\n<line x1="92.000000" y1="72.480000" x2="98.108418" y2="72.480000" style="stroke:rgb(0,0,255);stroke-width:0.50" />\n<line x1="97.108418" y1="14.000000" x2="97.108418" y2="72.480000" style="stroke:rgb(0,0,255);stroke-width:0.50" /> \n  <polygon points="97.108418,72.480000 98.108418,69.480000 97.108418,68.480000 96.108418,69.480000" style="fill:rgb(0,0,255);stroke:rgb(0,0,255);stroke-width:0" /><polygon points="97.108418,14.000000 96.108418,17.000000 97.108418,18.000000 98.108418,17.000000" style="fill:rgb(0,0,255);stroke:rgb(0,0,255);stroke-width:0" /> \n  <text x="95.108418" y="43.240000" font-family="inherit" font-size="3.6" fill="rgb(0,0,255)" text-anchor="middle" transform="rotate(-90.000000 95.108418,43.240000)" >731</text> </g>
  Visible = true
  X = 0
  Y = 0
  arrowL1 = 3
  arrowL2 = 1
  arrowW = 2
  arrow_scheme = 0
  autoPlaceOffset = 2
  autoPlaceText = true
  click1_x = 97.1084
  click1_y = 32.3695
  click2_x = 97.1084
  click2_y = 32.3695
  comma_decimal_place = false
  dimension_line_overshoot = 1
  gap_datum_points = 2
  halfDimension_linear = false
  lineColor = rgb(0,0,255)
  strokeWidth = 0.5
  textFormat_linear = %(value)3.3f
  textRenderer_color = rgb(0,0,255)
  textRenderer_family = inherit
  textRenderer_size = 3.6
  unit_custom_scale = 1
  unit_scheme = 0
FEATURE [Drawing::FeatureViewPython] dim030  # drawing view (typed FeaturePython)
  Rotation = 0
  ViewResult = <g> \n  <line x1="41.520000" y1="82.000000" x2="41.520000" y2="87.318593" style="stroke:rgb(0,0,255);stroke-width:0.50" />\n<line x1="96.000000" y1="82.000000" x2="96.000000" y2="87.318593" style="stroke:rgb(0,0,255);stroke-width:0.50" />\n<line x1="41.520000" y1="86.318593" x2="96.000000" y2="86.318593" style="stroke:rgb(0,0,255);stroke-width:0.50" /> \n  <polygon points="96.000000,86.318593 93.000000,85.318593 92.000000,86.318593 93.000000,87.318593" style="fill:rgb(0,0,255);stroke:rgb(0,0,255);stroke-width:0" /><polygon points="41.520000,86.318593 44.520000,87.318593 45.520000,86.318593 44.520000,85.318593" style="fill:rgb(0,0,255);stroke:rgb(0,0,255);stroke-width:0" /> \n  <text x="68.760000" y="84.318593" font-family="inherit" font-size="3.6" fill="rgb(0,0,255)" text-anchor="middle" transform="rotate(0.000000 68.760000,84.318593)" >681</text> </g>
  Visible = true
  X = 0
  Y = 0
  arrowL1 = 3
  arrowL2 = 1
  arrowW = 2
  arrow_scheme = 0
  autoPlaceOffset = 2
  autoPlaceText = true
  click1_x = 55.0849
  click1_y = 86.3186
  click2_x = 55.0849
  click2_y = 86.3186
  comma_decimal_place = false
  dimension_line_overshoot = 1
  gap_datum_points = 2
  halfDimension_linear = false
  lineColor = rgb(0,0,255)
  strokeWidth = 0.5
  textFormat_linear = %(value)3.3f
  textRenderer_color = rgb(0,0,255)
  textRenderer_family = inherit
  textRenderer_size = 3.6
  unit_custom_scale = 1
  unit_scheme = 0
FEATURE [Drawing::FeatureViewPython] dim031  # drawing view (typed FeaturePython)
  Rotation = 0
  ViewResult = <g> \n  <line x1="94.000000" y1="80.000000" x2="85.318593" y2="80.000000" style="stroke:rgb(0,0,255);stroke-width:0.50" />\n<line x1="94.000000" y1="104.000000" x2="85.318593" y2="104.000000" style="stroke:rgb(0,0,255);stroke-width:0.50" />\n<line x1="86.318593" y1="80.000000" x2="86.318593" y2="104.000000" style="stroke:rgb(0,0,255);stroke-width:0.50" /> \n  <polygon points="86.318593,104.000000 87.318593,101.000000 86.318593,100.000000 85.318593,101.000000" style="fill:rgb(0,0,255);stroke:rgb(0,0,255);stroke-width:0" /><polygon points="86.318593,80.000000 85.318593,83.000000 86.318593,84.000000 87.318593,83.000000" style="fill:rgb(0,0,255);stroke:rgb(0,0,255);stroke-width:0" /> \n  <text x="84.318593" y="92.000000" font-family="inherit" font-size="3.6" fill="rgb(0,0,255)" text-anchor="middle" transform="rotate(-90.000000 84.318593,92.000000)" >300</text> </g>
  Visible = true
  X = 0
  Y = 0
  arrowL1 = 3
  arrowL2 = 1
  arrowW = 2
  arrow_scheme = 0
  autoPlaceOffset = 2
  autoPlaceText = true
  click1_x = 86.3186
  click1_y = 91.9974
  click2_x = 86.3186
  click2_y = 91.9974
  comma_decimal_place = false
  dimension_line_overshoot = 1
  gap_datum_points = 2
  halfDimension_linear = false
  lineColor = rgb(0,0,255)
  strokeWidth = 0.5
  textFormat_linear = %(value)3.3f
  textRenderer_color = rgb(0,0,255)
  textRenderer_family = inherit
  textRenderer_size = 3.6
  unit_custom_scale = 1
  unit_scheme = 0
FEATURE [Drawing::FeatureViewPython] dim032  # drawing view (typed FeaturePython)
  Rotation = 0
  ViewResult = <g> \n  <line x1="85.000000" y1="108.600000" x2="85.000000" y2="115.144982" style="stroke:rgb(0,0,255);stroke-width:0.50" />\n<line x1="41.000000" y1="108.600000" x2="41.000000" y2="115.144982" style="stroke:rgb(0,0,255);stroke-width:0.50" />\n<line x1="85.000000" y1="114.144982" x2="41.000000" y2="114.144982" style="stroke:rgb(0,0,255);stroke-width:0.50" /> \n  <polygon points="41.000000,114.144982 44.000000,115.144982 45.000000,114.144982 44.000000,113.144982" style="fill:rgb(0,0,255);stroke:rgb(0,0,255);stroke-width:0" /><polygon points="85.000000,114.144982 82.000000,113.144982 81.000000,114.144982 82.000000,115.144982" style="fill:rgb(0,0,255);stroke:rgb(0,0,255);stroke-width:0" /> \n  <text x="63.000000" y="112.144982" font-family="inherit" font-size="3.6" fill="rgb(0,0,255)" text-anchor="middle" transform="rotate(0.000000 63.000000,112.144982)" >550</text> </g>
  Visible = true
  X = 0
  Y = 0
  arrowL1 = 3
  arrowL2 = 1
  arrowW = 2
  arrow_scheme = 0
  autoPlaceOffset = 2
  autoPlaceText = true
  click1_x = 63.0353
  click1_y = 114.145
  click2_x = 63.0353
  click2_y = 114.145
  comma_decimal_place = false
  dimension_line_overshoot = 1
  gap_datum_points = 2
  halfDimension_linear = false
  lineColor = rgb(0,0,255)
  strokeWidth = 0.5
  textFormat_linear = %(value)3.3f
  textRenderer_color = rgb(0,0,255)
  textRenderer_family = inherit
  textRenderer_size = 3.6
  unit_custom_scale = 1
  unit_scheme = 0
FEATURE [Drawing::FeatureViewPython] dim033  # drawing view (typed FeaturePython)
  Rotation = 0
  ViewResult = <g> \n  <line x1="43.000000" y1="163.000000" x2="50.973923" y2="163.000000" style="stroke:rgb(0,0,255);stroke-width:0.50" />\n<line x1="43.000000" y1="106.600000" x2="50.973923" y2="106.600000" style="stroke:rgb(0,0,255);stroke-width:0.50" />\n<line x1="49.973923" y1="163.000000" x2="49.973923" y2="106.600000" style="stroke:rgb(0,0,255);stroke-width:0.50" /> \n  <polygon points="49.973923,106.600000 48.973923,109.600000 49.973923,110.600000 50.973923,109.600000" style="fill:rgb(0,0,255);stroke:rgb(0,0,255);stroke-width:0" /><polygon points="49.973923,163.000000 50.973923,160.000000 49.973923,159.000000 48.973923,160.000000" style="fill:rgb(0,0,255);stroke:rgb(0,0,255);stroke-width:0" /> \n  <text x="47.973923" y="134.800000" font-family="inherit" font-size="3.6" fill="rgb(0,0,255)" text-anchor="middle" transform="rotate(-90.000000 47.973923,134.800000)" >705</text> </g>
  Visible = true
  X = 0
  Y = 0
  arrowL1 = 3
  arrowL2 = 1
  arrowW = 2
  arrow_scheme = 0
  autoPlaceOffset = 2
  autoPlaceText = true
  click1_x = 49.9739
  click1_y = 128.342
  click2_x = 49.9739
  click2_y = 128.342
  comma_decimal_place = false
  dimension_line_overshoot = 1
  gap_datum_points = 2
  halfDimension_linear = false
  lineColor = rgb(0,0,255)
  strokeWidth = 0.5
  textFormat_linear = %(value)3.3f
  textRenderer_color = rgb(0,0,255)
  textRenderer_family = inherit
  textRenderer_size = 3.6
  unit_custom_scale = 1
  unit_scheme = 0
FEATURE [Drawing::FeatureViewPython] dim034  # drawing view (typed FeaturePython)
  Rotation = 0
  ViewResult = <g> \n  <line x1="88.000000" y1="163.000000" x2="94.133219" y2="163.000000" style="stroke:rgb(0,0,255);stroke-width:0.50" />\n<line x1="88.000000" y1="106.600000" x2="94.133219" y2="106.600000" style="stroke:rgb(0,0,255);stroke-width:0.50" />\n<line x1="93.133219" y1="163.000000" x2="93.133219" y2="106.600000" style="stroke:rgb(0,0,255);stroke-width:0.50" /> \n  <polygon points="93.133219,106.600000 92.133219,109.600000 93.133219,110.600000 94.133219,109.600000" style="fill:rgb(0,0,255);stroke:rgb(0,0,255);stroke-width:0" /><polygon points="93.133219,163.000000 94.133219,160.000000 93.133219,159.000000 92.133219,160.000000" style="fill:rgb(0,0,255);stroke:rgb(0,0,255);stroke-width:0" /> \n  <text x="91.133219" y="134.800000" font-family="inherit" font-size="3.6" fill="rgb(0,0,255)" text-anchor="middle" transform="rotate(-90.000000 91.133219,134.800000)" >705</text> </g>
  Visible = true
  X = 0
  Y = 0
  arrowL1 = 3
  arrowL2 = 1
  arrowW = 2
  arrow_scheme = 0
  autoPlaceOffset = 2
  autoPlaceText = true
  click1_x = 93.1332
  click1_y = 122.095
  click2_x = 93.1332
  click2_y = 122.095
  comma_decimal_place = false
  dimension_line_overshoot = 1
  gap_datum_points = 2
  halfDimension_linear = false
  lineColor = rgb(0,0,255)
  strokeWidth = 0.5
  textFormat_linear = %(value)3.3f
  textRenderer_color = rgb(0,0,255)
  textRenderer_family = inherit
  textRenderer_size = 3.6
  unit_custom_scale = 1
  unit_scheme = 0
FEATURE [Drawing::FeatureViewPython] dim035  # drawing view (typed FeaturePython)
  Rotation = 0
  ViewResult = <g> \n  <line x1="103.520000" y1="108.600000" x2="103.520000" y2="115.144982" style="stroke:rgb(0,0,255);stroke-width:0.50" />\n<line x1="86.000000" y1="108.600000" x2="86.000000" y2="115.144982" style="stroke:rgb(0,0,255);stroke-width:0.50" />\n<line x1="103.520000" y1="114.144982" x2="86.000000" y2="114.144982" style="stroke:rgb(0,0,255);stroke-width:0.50" /> \n  <polygon points="86.000000,114.144982 89.000000,115.144982 90.000000,114.144982 89.000000,113.144982" style="fill:rgb(0,0,255);stroke:rgb(0,0,255);stroke-width:0" /><polygon points="103.520000,114.144982 100.520000,113.144982 99.520000,114.144982 100.520000,115.144982" style="fill:rgb(0,0,255);stroke:rgb(0,0,255);stroke-width:0" /> \n  <text x="94.760000" y="112.144982" font-family="inherit" font-size="3.6" fill="rgb(0,0,255)" text-anchor="middle" transform="rotate(0.000000 94.760000,112.144982)" >219</text> </g>
  Visible = true
  X = 0
  Y = 0
  arrowL1 = 3
  arrowL2 = 1
  arrowW = 2
  arrow_scheme = 0
  autoPlaceOffset = 2
  autoPlaceText = true
  click1_x = 91.9974
  click1_y = 114.145
  click2_x = 91.9974
  click2_y = 114.145
  comma_decimal_place = false
  dimension_line_overshoot = 1
  gap_datum_points = 2
  halfDimension_linear = false
  lineColor = rgb(0,0,255)
  strokeWidth = 0.5
  textFormat_linear = %(value)3.3f
  textRenderer_color = rgb(0,0,255)
  textRenderer_family = inherit
  textRenderer_size = 3.6
  unit_custom_scale = 1
  unit_scheme = 0
FEATURE [Drawing::FeatureViewPython] dim036  # drawing view (typed FeaturePython)
  Rotation = 0
  ViewResult = <g> \n  <line x1="113.000000" y1="110.520000" x2="113.000000" y2="117.984410" style="stroke:rgb(0,0,255);stroke-width:0.50" />\n<line x1="105.000000" y1="110.520000" x2="105.000000" y2="117.984410" style="stroke:rgb(0,0,255);stroke-width:0.50" />\n<line x1="113.000000" y1="116.984410" x2="105.000000" y2="116.984410" style="stroke:rgb(0,0,255);stroke-width:0.50" /> \n  <polygon points="105.000000,116.984410 102.000000,115.984410 101.000000,116.984410 102.000000,117.984410" style="fill:rgb(0,0,255);stroke:rgb(0,0,255);stroke-width:0" /><polygon points="113.000000,116.984410 116.000000,117.984410 117.000000,116.984410 116.000000,115.984410" style="fill:rgb(0,0,255);stroke:rgb(0,0,255);stroke-width:0" /> \n  <text x="109.000000" y="114.984410" font-family="inherit" font-size="3.6" fill="rgb(0,0,255)" text-anchor="middle" transform="rotate(0.000000 109.000000,114.984410)" >100</text> </g>
  Visible = true
  X = 0
  Y = 0
  arrowL1 = 3
  arrowL2 = 1
  arrowW = 2
  arrow_scheme = 0
  autoPlaceOffset = 2
  autoPlaceText = true
  click1_x = 106.195
  click1_y = 116.984
  click2_x = 106.195
  click2_y = 116.984
  comma_decimal_place = false
  dimension_line_overshoot = 1
  gap_datum_points = 2
  halfDimension_linear = false
  lineColor = rgb(0,0,255)
  strokeWidth = 0.5
  textFormat_linear = %(value)3.3f
  textRenderer_color = rgb(0,0,255)
  textRenderer_family = inherit
  textRenderer_size = 3.6
  unit_custom_scale = 1
  unit_scheme = 0
FEATURE [Drawing::FeatureViewPython] dim037  # drawing view (typed FeaturePython)
  Rotation = 0
  ViewResult = <g> \n  <line x1="107.000000" y1="108.520000" x2="111.737669" y2="108.520000" style="stroke:rgb(0,0,255);stroke-width:0.50" />\n<line x1="107.000000" y1="163.000000" x2="111.737669" y2="163.000000" style="stroke:rgb(0,0,255);stroke-width:0.50" />\n<line x1="110.737669" y1="108.520000" x2="110.737669" y2="163.000000" style="stroke:rgb(0,0,255);stroke-width:0.50" /> \n  <polygon points="110.737669,163.000000 111.737669,160.000000 110.737669,159.000000 109.737669,160.000000" style="fill:rgb(0,0,255);stroke:rgb(0,0,255);stroke-width:0" /><polygon points="110.737669,108.520000 109.737669,111.520000 110.737669,112.520000 111.737669,111.520000" style="fill:rgb(0,0,255);stroke:rgb(0,0,255);stroke-width:0" /> \n  <text x="108.737669" y="135.760000" font-family="inherit" font-size="3.6" fill="rgb(0,0,255)" text-anchor="middle" transform="rotate(-90.000000 108.737669,135.760000)" >681</text> </g>
  Visible = true
  X = 0
  Y = 0
  arrowL1 = 3
  arrowL2 = 1
  arrowW = 2
  arrow_scheme = 0
  autoPlaceOffset = 2
  autoPlaceText = true
  click1_x = 110.738
  click1_y = 132.317
  click2_x = 110.738
  click2_y = 132.317
  comma_decimal_place = false
  dimension_line_overshoot = 1
  gap_datum_points = 2
  halfDimension_linear = false
  lineColor = rgb(0,0,255)
  strokeWidth = 0.5
  textFormat_linear = %(value)3.3f
  textRenderer_color = rgb(0,0,255)
  textRenderer_family = inherit
  textRenderer_size = 3.6
  unit_custom_scale = 1
  unit_scheme = 0
FEATURE [Drawing::FeatureViewPython] dim042  # drawing view (typed FeaturePython)
  Rotation = 0
  ViewResult = <g> \n  <line x1="41.480000" y1="166.400000" x2="41.480000" y2="173.069301" style="stroke:rgb(0,0,255);stroke-width:0.50" />\n<line x1="103.000000" y1="166.400000" x2="103.000000" y2="173.069301" style="stroke:rgb(0,0,255);stroke-width:0.50" />\n<line x1="41.480000" y1="172.069301" x2="103.000000" y2="172.069301" style="stroke:rgb(0,0,255);stroke-width:0.50" /> \n  <polygon points="103.000000,172.069301 100.000000,171.069301 99.000000,172.069301 100.000000,173.069301" style="fill:rgb(0,0,255);stroke:rgb(0,0,255);stroke-width:0" /><polygon points="41.480000,172.069301 44.480000,173.069301 45.480000,172.069301 44.480000,171.069301" style="fill:rgb(0,0,255);stroke:rgb(0,0,255);stroke-width:0" /> \n  <text x="72.240000" y="170.069301" font-family="inherit" font-size="3.6" fill="rgb(0,0,255)" text-anchor="middle" transform="rotate(0.000000 72.240000,170.069301)" >769</text> </g>
  Visible = true
  X = 0
  Y = 0
  arrowL1 = 3
  arrowL2 = 1
  arrowW = 2
  arrow_scheme = 0
  autoPlaceOffset = 2
  autoPlaceText = true
  click1_x = 64.1711
  click1_y = 172.069
  click2_x = 64.1711
  click2_y = 172.069
  comma_decimal_place = false
  dimension_line_overshoot = 1
  gap_datum_points = 2
  halfDimension_linear = false
  lineColor = rgb(0,0,255)
  strokeWidth = 0.5
  textFormat_linear = %(value)3.3f
  textRenderer_color = rgb(0,0,255)
  textRenderer_family = inherit
  textRenderer_size = 3.6
  unit_custom_scale = 1
  unit_scheme = 0
FEATURE [Drawing::FeatureViewPython] dim043  # drawing view (typed FeaturePython)
  Rotation = 0
  ViewResult = <g> \n  <line x1="101.000000" y1="164.400000" x2="90.997448" y2="164.400000" style="stroke:rgb(0,0,255);stroke-width:0.50" />\n<line x1="101.000000" y1="212.000000" x2="90.997448" y2="212.000000" style="stroke:rgb(0,0,255);stroke-width:0.50" />\n<line x1="91.997448" y1="164.400000" x2="91.997448" y2="212.000000" style="stroke:rgb(0,0,255);stroke-width:0.50" /> \n  <polygon points="91.997448,212.000000 92.997448,209.000000 91.997448,208.000000 90.997448,209.000000" style="fill:rgb(0,0,255);stroke:rgb(0,0,255);stroke-width:0" /><polygon points="91.997448,164.400000 90.997448,167.400000 91.997448,168.400000 92.997448,167.400000" style="fill:rgb(0,0,255);stroke:rgb(0,0,255);stroke-width:0" /> \n  <text x="89.997448" y="188.200000" font-family="inherit" font-size="3.6" fill="rgb(0,0,255)" text-anchor="middle" transform="rotate(-90.000000 89.997448,188.200000)" >595</text> </g>
  Visible = true
  X = 0
  Y = 0
  arrowL1 = 3
  arrowL2 = 1
  arrowW = 2
  arrow_scheme = 0
  autoPlaceOffset = 2
  autoPlaceText = true
  click1_x = 91.9974
  click1_y = 186.834
  click2_x = 91.9974
  click2_y = 186.834
  comma_decimal_place = false
  dimension_line_overshoot = 1
  gap_datum_points = 2
  halfDimension_linear = false
  lineColor = rgb(0,0,255)
  strokeWidth = 0.5
  textFormat_linear = %(value)3.3f
  textRenderer_color = rgb(0,0,255)
  textRenderer_family = inherit
  textRenderer_size = 3.6
  unit_custom_scale = 1
  unit_scheme = 0
FEATURE [Drawing::FeaturePage] Page004  label="Schnittplan"
  EditableTexts = Manuel Dillmann | PC-Schrank | Schnittplan | A4 | 5 / X | 0.08 | ... | ... | 18/04/2019 | REV A
  Group = -> [Ortho010,Ortho011,text011,Ortho012,text012,Ortho013,text013,Ortho014,text014,Ortho015,text015,Ortho016,text016,Ortho017,text017,Ortho018,text018,dim022,dim023,dim038,dim039,dim040,dim041,Ortho019,text019,Ortho020,text020,dim024,dim025,dim026,dim027,dim028,dim029,dim030,dim031,dim032,dim033,dim034,dim035,dim036,dim037,dim042,dim043]
  Template = C:/Program Files/FreeCAD 0.17/data/Mod/Drawing/Templates/A4_Portrait_ISO7200.svg
